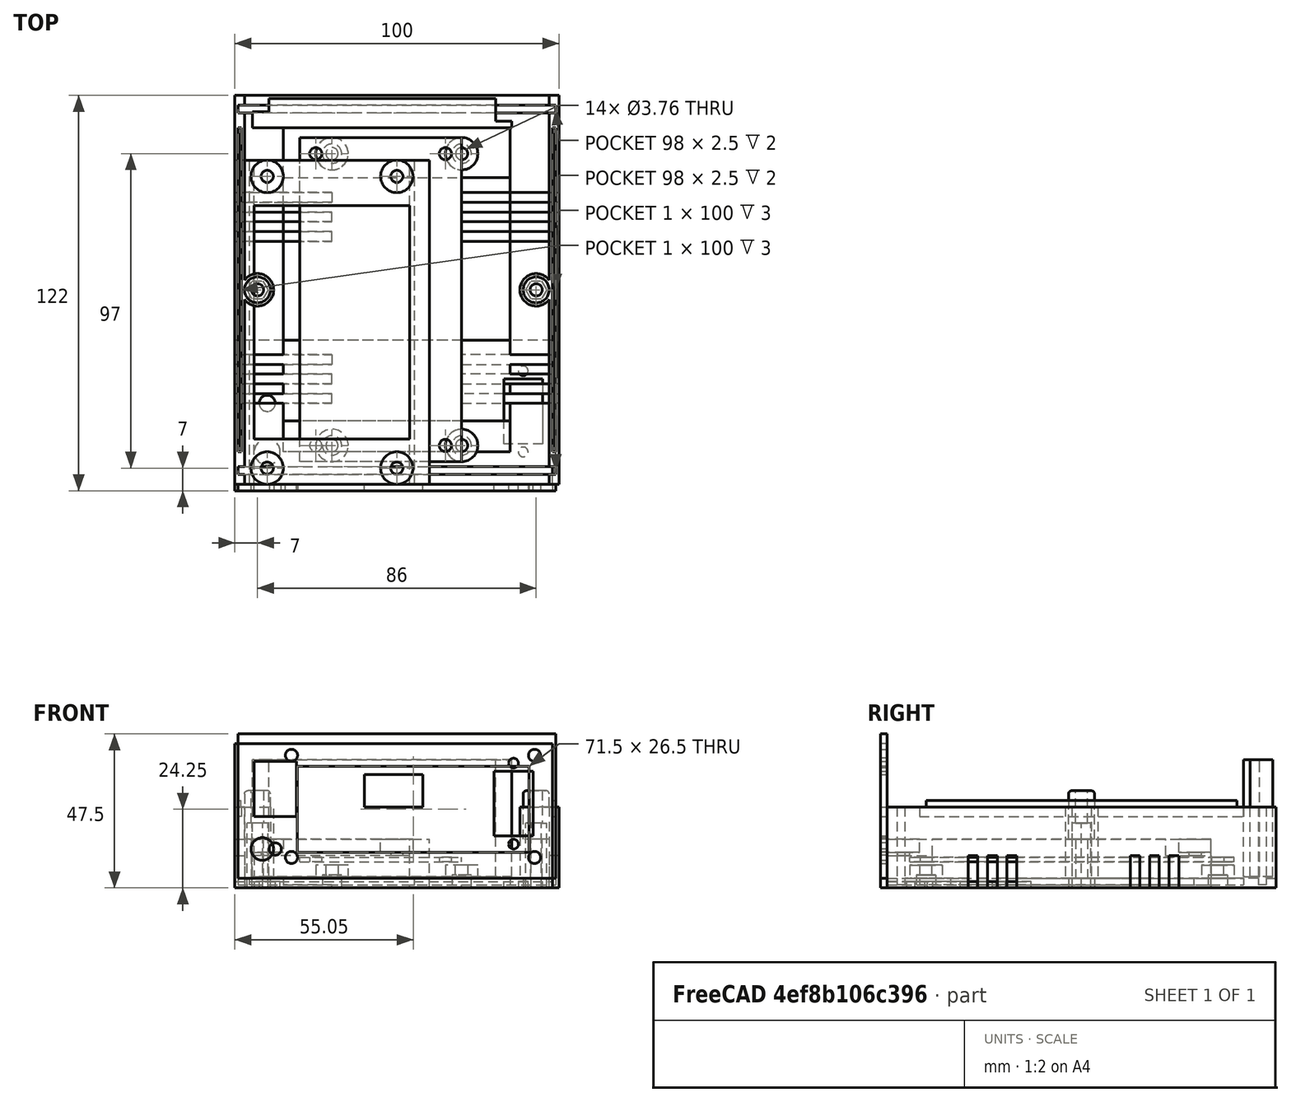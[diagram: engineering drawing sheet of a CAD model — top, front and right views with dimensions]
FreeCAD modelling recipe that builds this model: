
FCSTD DOCUMENT  (FreeCAD 0.18R)
Label: Gehäuse_mit_Display
License: All rights reserved
LicenseURL: http://en.wikipedia.org/wiki/All_rights_reserved
objects: Sketcher::SketchObject×35, PartDesign::Pocket×24, PartDesign::Pad×12, PartDesign::Body×9, PartDesign::Plane×8, PartDesign::FeatureBase×2, Spreadsheet::Sheet×1, PartDesign::Fillet×1
note: 127 computed .brp shape members not serialized (recipe doc carries the construction recipe); baked Part::Feature solids carry a one-line shape summary decoded from their .brp

FEATURE [Sketcher::SketchObject] Sketch
  MapMode = 5
  Support = -> [XY_Plane]
  expr: Constraints.Grund_X = Parameter.Breite
  expr: Constraints.Grund_Y = Parameter.Tiefe
  sketch-geometry (4):
    g0: LineSegment StartX=0 StartY=120 StartZ=0 EndX=100 EndY=120 EndZ=0
    g1: LineSegment StartX=100 StartY=120 StartZ=0 EndX=100 EndY=0 EndZ=0
    g2: LineSegment StartX=100 StartY=0 StartZ=0 EndX=0 EndY=0 EndZ=0
    g3: LineSegment StartX=0 StartY=0 StartZ=0 EndX=0 EndY=120 EndZ=0
  constraints (11):
    c: Coincident(g0,g1)
    c: Coincident(g1,g2)
    c: Coincident(g2,g3)
    c: Coincident(g3,g0)
    c: Horizontal(g2)
    c: Vertical(g1)
    c: DistanceY(g2,g0) = 120  'Grund_Y'
    c: DistanceX(g2,g1) = 100  'Grund_X'
    c: Vertical(g3)
    c: Horizontal(g0)
    c: Coincident(g-1,g2)
FEATURE [Spreadsheet::Sheet] Spreadsheet  label="Parameter"
  cells = A1=Breite (X); B1(Breite)=100; A2=Tiefe (Y); B2(Tiefe)=120; A3=Höhe (Z); B3(Hoehe)=25; A4=Wandstärke; B4(Wandstaerke)=3; A5=Wandstärke Frontblende; B5(Wandstaerke_Frontblende)=2.5; A6=Breite der Nut / Feder zwischen Ober und Unterteil; B6(Nut_Feder_Breite)=1; A7=Faktor Breite Feder zwischen Ober-und Unterteil; B7(Nut_Feder_Breite_Faktor_Unterteil)=0.90000000000000002; A8=Start der Nut von der Front- Heckansicht; B8(Nut_Feder_Entfernung_Vorne_Hinten)=10; A9=Entfernung Schalenverschraubung zur Innenwand; B9(Abstand_Verschraubung_Innen)=4; A10=Breite Platine; B10(Platine_Breite)=50; A11=Tiefe Platine; B11(Platine_Tiefe)=100; A12=Abstand Bohrlöcher Platine zum Außenrand; B12(Platine_Abstand_Bohrloch_Aussenrand)=5; A13=Breite Luftschlitz Boden; B13(Luftschlitz_Breite_Boden)=30; A14=Tiefe Luftschlitz Boden; B14(Luftschlitz_Tiefe_Boden)=3; A15=Höhe Luftschlitz Boden; B15(Luftschlitz_Hoehe_Boden)=10; A17=Helper; A18=Abstand Schalenverschraubung außen; B18(Helper_Abstand_Schalenverschraubung_Aussen)==Abstand_Verschraubung_Innen + Wandstaerke; A19=Breite Feder Unterteil; B19(Helper_Nut_Feder_Breite_Unterteil)==Parameter.Nut_Feder_Breite * Parameter.Nut_Feder_Breite_Faktor_Unterteil
FEATURE [PartDesign::Pad] Pad  label="Grundkörper"
  Length = 25
  Length2 = 100
  Profile = -> Sketch
  Type = 0
  expr: Length = Parameter.Hoehe
FEATURE [Sketcher::SketchObject] Sketch002
  MapMode = 5
  Support = -> [XY_Plane001]
  sketch-geometry (8):
    g0: LineSegment StartX=0 StartY=0 StartZ=0 EndX=80 EndY=0 EndZ=0
    g1: LineSegment StartX=80 StartY=0 StartZ=0 EndX=80 EndY=2 EndZ=0
    g2: LineSegment StartX=80 StartY=2 StartZ=0 EndX=75 EndY=2 EndZ=0
    g3: LineSegment StartX=75 StartY=2 StartZ=0 EndX=75 EndY=9 EndZ=0
    g4: LineSegment StartX=75 StartY=9 StartZ=0 EndX=5 EndY=9 EndZ=0
    g5: LineSegment StartX=5 StartY=9 StartZ=0 EndX=5 EndY=5 EndZ=0
    g6: LineSegment StartX=5 StartY=5 StartZ=0 EndX=0 EndY=5 EndZ=0
    g7: LineSegment StartX=0 StartY=5 StartZ=0 EndX=0 EndY=0 EndZ=0
  constraints (23):
    c: Horizontal(g0)
    c: Coincident(g0,g1)
    c: Coincident(g1,g2)
    c: Horizontal(g2)
    c: Coincident(g2,g3)
    c: Vertical(g3)
    c: Coincident(g3,g4)
    c: Horizontal(g4)
    c: Coincident(g4,g5)
    c: Vertical(g5)
    c: Coincident(g5,g6)
    c: Horizontal(g6)
    c: Coincident(g6,g7)
    c: Coincident(g7,g0)
    c: Vertical(g7)
    c: DistanceY(g0,g6) = 5
    c: DistanceY(g0,g1) = 2
    c: DistanceX(g0,g0) = 80
    c: Vertical(g1)
    c: DistanceX(g4,g3) = 70
    c: DistanceY(g2,g3) = 7
    c: DistanceX(g6,g5) = 5
    c: Coincident(g-1,g0)
FEATURE [PartDesign::Pad] Pad001
  Length = 35
  Length2 = 100
  Profile = -> Sketch002
  Type = 0
FEATURE [PartDesign::Pad] Pad002
  BaseFeature = -> Pad001
  Length = 36
  Length2 = 100
  Profile = -> Sketch002
  Type = 0
FEATURE [PartDesign::Body] Body001  label="LCD1602 Display"
  Group = -> [Sketch002,Pad001,Pad002]
  Origin = -> Origin001
  Placement = pos=(5.5,110,3.5) rot=(0,0,1;0rad)
  Tip = -> Pad002
FEATURE [Sketcher::SketchObject] Sketch003
  MapMode = 5
  Placement = pos=(0,0,0) rot=(1,0,0;1.5708rad)
  Support = -> [XZ_Plane]
  expr: Constraints[11] = Parameter.Hoehe - 1 * Parameter.Wandstaerke
  expr: Constraints[10] = Parameter.Wandstaerke
  expr: Constraints[9] = Parameter.Breite - 2 * Parameter.Wandstaerke
  expr: Constraints[8] = Parameter.Wandstaerke
  sketch-geometry (4):
    g0: LineSegment StartX=3 StartY=25 StartZ=0 EndX=97 EndY=25 EndZ=0
    g1: LineSegment StartX=97 StartY=25 StartZ=0 EndX=97 EndY=3 EndZ=0
    g2: LineSegment StartX=97 StartY=3 StartZ=0 EndX=3 EndY=3 EndZ=0
    g3: LineSegment StartX=3 StartY=3 StartZ=0 EndX=3 EndY=25 EndZ=0
  constraints (12):
    c: Coincident(g0,g1)
    c: Coincident(g1,g2)
    c: Coincident(g2,g3)
    c: Coincident(g3,g0)
    c: Horizontal(g0)
    c: Horizontal(g2)
    c: Vertical(g1)
    c: Vertical(g3)
    c: DistanceX(g-1,g2) = 3
    c: DistanceX(g2,g1) = 94
    c: DistanceY(g-1,g2) = 3
    c: DistanceY(g1,g0) = 22
FEATURE [Sketcher::SketchObject] Sketch001
  MapMode = 5
  Placement = pos=(0,0,25) rot=(0,0,1;0rad)
  Support = -> [Pad]
  expr: Constraints[39] = Parameter.Wandstaerke_Frontblende
  expr: Constraints[21] = Parameter.Breite
  expr: Constraints[31] = Parameter.Wandstaerke
  expr: Constraints[50] = Parameter.Wandstaerke_Frontblende
  expr: Constraints[36] = Parameter.Wandstaerke
  expr: Constraints[34] = Parameter.Wandstaerke
  expr: Constraints[58] = Parameter.Wandstaerke_Frontblende
  expr: Constraints[20] = Parameter.Tiefe
  expr: Constraints[38] = Parameter.Wandstaerke
  expr: Constraints[37] = Parameter.Wandstaerke
  expr: Constraints[35] = Parameter.Wandstaerke
  expr: Constraints[56] = Parameter.Wandstaerke_Frontblende
  expr: Constraints[23] = Parameter.Wandstaerke
  sketch-geometry (20):
    g0: LineSegment StartX=3 StartY=117 StartZ=0 EndX=1 EndY=117 EndZ=0
    g1: LineSegment StartX=1 StartY=117 StartZ=0 EndX=1 EndY=114.5 EndZ=0
    g2: LineSegment StartX=1 StartY=114.5 StartZ=0 EndX=3 EndY=114.5 EndZ=0
    g3: LineSegment StartX=3 StartY=5.5 StartZ=0 EndX=1 EndY=5.5 EndZ=0
    g4: LineSegment StartX=1 StartY=5.5 StartZ=0 EndX=1 EndY=3 EndZ=0
    g5: LineSegment StartX=1 StartY=3 StartZ=0 EndX=3 EndY=3 EndZ=0
    g6: LineSegment StartX=3 StartY=3 StartZ=0 EndX=97 EndY=3 EndZ=0
    g7: LineSegment StartX=97 StartY=3 StartZ=0 EndX=99 EndY=3 EndZ=0
    g8: LineSegment StartX=99 StartY=3 StartZ=0 EndX=99 EndY=5.5 EndZ=0
    g9: LineSegment StartX=99 StartY=5.5 StartZ=0 EndX=97 EndY=5.5 EndZ=0
    g10: LineSegment StartX=97 StartY=114.5 StartZ=0 EndX=99 EndY=114.5 EndZ=0
    g11: LineSegment StartX=99 StartY=114.5 StartZ=0 EndX=99 EndY=117 EndZ=0
    g12: LineSegment StartX=99 StartY=117 StartZ=0 EndX=97 EndY=117 EndZ=0
    g13: LineSegment StartX=97 StartY=117 StartZ=0 EndX=3 EndY=117 EndZ=0
    g14: LineSegment [constr] StartX=-3e-16 StartY=0 StartZ=0 EndX=100 EndY=0 EndZ=0
    g15: LineSegment [constr] StartX=100 StartY=0 StartZ=0 EndX=100 EndY=120 EndZ=0
    g16: LineSegment [constr] StartX=100 StartY=120 StartZ=0 EndX=0 EndY=120 EndZ=0
    g17: LineSegment StartX=3 StartY=114.5 StartZ=0 EndX=3 EndY=5.5 EndZ=0
    g18: LineSegment StartX=97 StartY=114.5 StartZ=0 EndX=97 EndY=5.5 EndZ=0
    g19: LineSegment [constr] StartX=0 StartY=120 StartZ=0 EndX=0 EndY=0 EndZ=0
  constraints (59):
    c: Coincident(g0,g1)
    c: Vertical(g1)
    c: Coincident(g1,g2)
    c: Horizontal(g2)
    c: Horizontal(g3)
    c: Coincident(g3,g4)
    c: Vertical(g4)
    c: Coincident(g4,g5)
    c: Horizontal(g6)
    c: Horizontal(g7)
    c: Coincident(g7,g8)
    c: Coincident(g8,g9)
    c: Horizontal(g10)
    c: Coincident(g10,g11)
    c: Coincident(g11,g12)
    c: Horizontal(g13)
    c: Coincident(g14,g15)
    c: Coincident(g15,g16)
    c: Horizontal(g14)
    c: Horizontal(g16)
    c: DistanceY(g14,g15) = 120
    c: DistanceX(g16,g15) = 100
    c: Coincident(g14,g-1)
    c: DistanceY(g-1,g6) = 3
    c: Horizontal(g5)
    c: Horizontal(g12)
    c: Vertical(g11)
    c: Vertical(g8)
    c: DistanceX(g-1,g4) = 1
    c: DistanceX(g16,g0) = 1
    c: Horizontal(g0)
    c: DistanceX(g-1,g3) = 3
    c: DistanceX(g7,g14) = 1
    c: Horizontal(g9)
    c: DistanceX(g9,g14) = 3
    c: DistanceX(g-1,g6) = 3
    c: DistanceX(g6,g14) = 3
    c: DistanceX(g16,g13) = 3
    c: DistanceX(g13,g15) = 3
    c: DistanceY(g2,g0) = 2.5
    c: Vertical(g17)
    c: Coincident(g2,g17)
    c: Coincident(g18,g10)
    c: Coincident(g18,g9)
    c: Vertical(g18)
    c: Equal(g16,g14)
    c: Coincident(g17,g3)
    c: Coincident(g19,g-1)
    c: Coincident(g19,g16)
    c: DistanceX(g11,g15) = 1
    c: DistanceY(g10,g11) = 2.5
    c: Equal(g0,g2)
    c: DistanceY(g0,g16) = 3
    c: Coincident(g13,g0)
    c: Coincident(g13,g12)
    c: Coincident(g5,g6)
    c: DistanceY(g4,g3) = 2.5
    c: Coincident(g7,g6)
    c: DistanceY(g7,g8) = 2.5
FEATURE [PartDesign::Pocket] Pocket  label="Innenraum"
  BaseFeature = -> Pad
  Length = 22
  Length2 = 100
  Profile = -> Sketch001
  Type = 0
  expr: Length = Parameter.Hoehe - Parameter.Wandstaerke
FEATURE [PartDesign::Pocket] Pocket001  label="Öffnung vorn und hinten"
  BaseFeature = -> Pocket
  Length = 5
  Length2 = 100
  Profile = -> Sketch003
  Type = 1
FEATURE [Sketcher::SketchObject] Sketch005
  MapMode = 5
  Placement = pos=(0,0,3) rot=(0,0,1;0rad)
  Support = -> [Pocket001]
  expr: Constraints[23] = Parameter.Wandstaerke
  expr: Constraints[21] = Parameter.Wandstaerke_Frontblende
  expr: Constraints[11] = Parameter.Tiefe - Parameter.Wandstaerke_Frontblende - Parameter.Wandstaerke
  expr: Constraints[10] = Parameter.Wandstaerke_Frontblende
  expr: Constraints[22] = Parameter.Breite - 2
  expr: Constraints[9] = Parameter.Breite - 2
  sketch-geometry (8):
    g0: LineSegment StartX=1 StartY=117 StartZ=0 EndX=99 EndY=117 EndZ=0
    g1: LineSegment StartX=99 StartY=117 StartZ=0 EndX=99 EndY=114.5 EndZ=0
    g2: LineSegment StartX=99 StartY=114.5 StartZ=0 EndX=1 EndY=114.5 EndZ=0
    g3: LineSegment StartX=1 StartY=114.5 StartZ=0 EndX=1 EndY=117 EndZ=0
    g4: LineSegment StartX=1 StartY=5.5 StartZ=0 EndX=99 EndY=5.5 EndZ=0
    g5: LineSegment StartX=99 StartY=5.5 StartZ=0 EndX=99 EndY=3 EndZ=0
    g6: LineSegment StartX=99 StartY=3 StartZ=0 EndX=1 EndY=3 EndZ=0
    g7: LineSegment StartX=1 StartY=3 StartZ=0 EndX=1 EndY=5.5 EndZ=0
  constraints (24):
    c: Coincident(g0,g1)
    c: Coincident(g1,g2)
    c: Coincident(g2,g3)
    c: Coincident(g3,g0)
    c: Horizontal(g0)
    c: Horizontal(g2)
    c: Vertical(g1)
    c: Vertical(g3)
    c: DistanceX(g-1,g2) = 1
    c: DistanceX(g0,g0) = 98
    c: DistanceY(g2,g0) = 2.5
    c: DistanceY(g-1,g2) = 114.5
    c: Coincident(g4,g5)
    c: Coincident(g5,g6)
    c: Coincident(g6,g7)
    c: Coincident(g7,g4)
    c: Horizontal(g4)
    c: Horizontal(g6)
    c: Vertical(g5)
    c: Vertical(g7)
    c: DistanceX(g-1,g6) = 1
    c: DistanceY(g5,g4) = 2.5
    c: DistanceX(g6,g5) = 98
    c: DistanceY(g-1,g6) = 3
FEATURE [Sketcher::SketchObject] Sketch006
  MapMode = 5
  Support = -> [XY_Plane002]
  sketch-geometry (4):
    g0: LineSegment StartX=0 StartY=100 StartZ=0 EndX=50 EndY=100 EndZ=0
    g1: LineSegment StartX=50 StartY=100 StartZ=0 EndX=50 EndY=0 EndZ=0
    g2: LineSegment StartX=50 StartY=0 StartZ=0 EndX=0 EndY=0 EndZ=0
    g3: LineSegment StartX=0 StartY=0 StartZ=0 EndX=0 EndY=100 EndZ=0
  constraints (11):
    c: Coincident(g0,g1)
    c: Coincident(g1,g2)
    c: Coincident(g2,g3)
    c: Coincident(g3,g0)
    c: Horizontal(g0)
    c: Horizontal(g2)
    c: Vertical(g1)
    c: Vertical(g3)
    c: DistanceY(g1,g0) = 100
    c: DistanceX(g2,g1) = 50
    c: Coincident(g-1,g2)
FEATURE [PartDesign::Pad] Pad003  label="Grundplatte"
  Length = 1.5
  Length2 = 100
  Profile = -> Sketch006
  Type = 0
FEATURE [Sketcher::SketchObject] Sketch008
  MapMode = 5
  Support = -> [XY_Plane002]
  sketch-geometry (12):
    g0: Circle CenterX=45 CenterY=95 CenterZ=0 NormalX=0 NormalY=0 NormalZ=1 AngleXU=0 Radius=1.88
    g1: Circle CenterX=5 CenterY=5 CenterZ=0 NormalX=0 NormalY=0 NormalZ=1 AngleXU=0 Radius=1.88
    g2: Circle CenterX=45 CenterY=5 CenterZ=0 NormalX=0 NormalY=0 NormalZ=1 AngleXU=0 Radius=1.88
    g3: LineSegment [constr] StartX=0 StartY=100 StartZ=0 EndX=50 EndY=100 EndZ=0
    g4: LineSegment [constr] StartX=50 StartY=100 StartZ=0 EndX=50 EndY=0 EndZ=0
    g5: LineSegment [constr] StartX=50 StartY=0 StartZ=0 EndX=0 EndY=0 EndZ=0
    g6: LineSegment [constr] StartX=0 StartY=0 StartZ=0 EndX=0 EndY=100 EndZ=0
    g7: LineSegment [constr] StartX=5 StartY=95 StartZ=0 EndX=45 EndY=95 EndZ=0
    g8: LineSegment [constr] StartX=45 StartY=95 StartZ=0 EndX=45 EndY=5 EndZ=0
    g9: LineSegment [constr] StartX=45 StartY=5 StartZ=0 EndX=5 EndY=5 EndZ=0
    g10: LineSegment [constr] StartX=5 StartY=5 StartZ=0 EndX=5 EndY=95 EndZ=0
    g11: Circle CenterX=5 CenterY=95 CenterZ=0 NormalX=0 NormalY=0 NormalZ=1 AngleXU=0 Radius=1.88
  constraints (31):
    c: Coincident(g3,g4)
    c: Coincident(g4,g5)
    c: Coincident(g5,g6)
    c: Coincident(g6,g3)
    c: Horizontal(g3)
    c: Horizontal(g5)
    c: Vertical(g4)
    c: Vertical(g6)
    c: Coincident(g5,g-1)
    c: DistanceY(g4,g3) = 100
    c: DistanceX(g-1,g4) = 50
    c: Coincident(g7,g8)
    c: Coincident(g8,g9)
    c: Coincident(g9,g10)
    c: Coincident(g10,g7)
    c: Horizontal(g7)
    c: Horizontal(g9)
    c: Vertical(g8)
    c: Vertical(g10)
    c: Coincident(g1,g9)
    c: Coincident(g8,g2)
    c: Coincident(g0,g7)
    c: DistanceX(g-1,g1) = 5
    c: DistanceY(g-1,g1) = 5
    c: DistanceX(g1,g2) = 40
    c: Coincident(g7,g11)
    c: Radius(g11) = 1.88
    c: Equal(g11,g0)
    c: Equal(g11,g1)
    c: Equal(g11,g2)
    c: DistanceY(g11,g3) = 5
FEATURE [PartDesign::Pocket] Pocket003  label="Befestigung M3"
  BaseFeature = -> Pad003
  Length = 12
  Length2 = 100
  Profile = -> Sketch008
  Reversed = true
  Type = 1
FEATURE [PartDesign::Body] Body002  label="Board"
  Group = -> [Sketch006,Pad003,Sketch008,Pocket003]
  Origin = -> Origin002
  Placement = pos=(20,7,8) rot=(0,0,1;0rad)
  Tip = -> Pocket003
FEATURE [Sketcher::SketchObject] Sketch010
  MapMode = 5
  Placement = pos=(-2e-16,-1.8e-15,7) rot=(0,0,1;0rad)
  expr: Constraints[11] = Parameter.Platine_Breite - 2 * Parameter.Platine_Abstand_Bohrloch_Aussenrand
  expr: Constraints[10] = Parameter.Platine_Tiefe - 2 * Parameter.Platine_Abstand_Bohrloch_Aussenrand
  expr: Constraints[8] = (Parameter.Breite - (Parameter.Platine_Breite - 2 * Parameter.Platine_Abstand_Bohrloch_Aussenrand)) / 2
  sketch-geometry (8):
    g0: LineSegment [constr] StartX=30 StartY=102 StartZ=0 EndX=70 EndY=102 EndZ=0
    g1: LineSegment [constr] StartX=70 StartY=102 StartZ=0 EndX=70 EndY=12 EndZ=0
    g2: LineSegment [constr] StartX=70 StartY=12 StartZ=0 EndX=30 EndY=12 EndZ=0
    g3: LineSegment [constr] StartX=30 StartY=12 StartZ=0 EndX=30 EndY=102 EndZ=0
    g4: Circle CenterX=30 CenterY=102 CenterZ=0 NormalX=0 NormalY=0 NormalZ=1 AngleXU=0 Radius=1.88
    g5: Circle CenterX=70 CenterY=102 CenterZ=0 NormalX=0 NormalY=0 NormalZ=1 AngleXU=0 Radius=1.88
    g6: Circle CenterX=30 CenterY=12 CenterZ=0 NormalX=0 NormalY=0 NormalZ=1 AngleXU=0 Radius=1.88
    g7: Circle CenterX=70 CenterY=12 CenterZ=0 NormalX=0 NormalY=0 NormalZ=1 AngleXU=0 Radius=1.88
  constraints (20):
    c: Coincident(g0,g1)
    c: Coincident(g1,g2)
    c: Coincident(g2,g3)
    c: Coincident(g3,g0)
    c: Horizontal(g0)
    c: Horizontal(g2)
    c: Vertical(g1)
    c: Vertical(g3)
    c: DistanceX(g-1,g2) = 30
    c: DistanceY(g-1,g2) = 12
    c: DistanceY(g1,g0) = 90
    c: DistanceX(g0,g0) = 40
    c: Equal(g4,g5)
    c: Equal(g4,g6)
    c: Equal(g4,g7)
    c: Radius(g4) = 1.88
    c: Coincident(g0,g4)
    c: Coincident(g0,g5)
    c: Coincident(g1,g7)
    c: Coincident(g2,g6)
FEATURE [PartDesign::Plane] DatumPlane  label="Ebene Boden innen"
  Length = 133.917
  MapMode = 5
  Placement = pos=(0,0,3) rot=(0,0,1;0rad)
  ResizeMode = 0
  Support = -> [Pocket001]
  Width = 153.917
FEATURE [Sketcher::SketchObject] Sketch009
  MapMode = 5
  Placement = pos=(0,0,3) rot=(0,0,1;0rad)
  Support = -> [DatumPlane]
  expr: Constraints[18] = Parameter.Helper_Abstand_Schalenverschraubung_Aussen
  expr: Constraints[3] = Parameter.Helper_Abstand_Schalenverschraubung_Aussen
  expr: Constraints[17] = Parameter.Tiefe
  expr: Constraints[16] = Parameter.Breite
  expr: Constraints[2] = Parameter.Tiefe / 2
  sketch-geometry (7):
    g0: Circle CenterX=7 CenterY=60 CenterZ=0 NormalX=0 NormalY=0 NormalZ=1 AngleXU=0 Radius=5
    g1: Circle CenterX=93 CenterY=60 CenterZ=0 NormalX=0 NormalY=0 NormalZ=1 AngleXU=0 Radius=5
    g2: LineSegment [constr] StartX=7 StartY=60 StartZ=0 EndX=93 EndY=60 EndZ=0
    g3: LineSegment [constr] StartX=0 StartY=120 StartZ=0 EndX=100 EndY=120 EndZ=0
    g4: LineSegment [constr] StartX=100 StartY=120 StartZ=0 EndX=100 EndY=0 EndZ=0
    g5: LineSegment [constr] StartX=100 StartY=0 StartZ=0 EndX=0 EndY=0 EndZ=0
    g6: LineSegment [constr] StartX=0 StartY=0 StartZ=0 EndX=0 EndY=120 EndZ=0
  constraints (19):
    c: Radius(g0) = 5
    c: Horizontal(g2)
    c: DistanceY(g-1,g2) = 60
    c: DistanceX(g-1,g2) = 7
    c: Coincident(g2,g0)
    c: Coincident(g1,g2)
    c: Equal(g0,g1)
    c: Coincident(g3,g4)
    c: Coincident(g4,g5)
    c: Coincident(g5,g6)
    c: Coincident(g6,g3)
    c: Horizontal(g3)
    c: Horizontal(g5)
    c: Vertical(g4)
    c: Vertical(g6)
    c: Coincident(g5,g-1)
    c: DistanceX(g-1,g4) = 100
    c: DistanceY(g4,g3) = 120
    c: DistanceX(g1,g4) = 7
FEATURE [PartDesign::Pad] Pad007  label="Gehäuseverschraubung"
  BaseFeature = -> Pocket001
  Length = 22
  Length2 = 100
  Profile = -> Sketch009
  Type = 0
  expr: Length = Parameter.Hoehe - Parameter.Wandstaerke
FEATURE [PartDesign::Plane] DatumPlane001  label="Ebene Unterseite001"
  Length = 133.917
  MapMode = 5
  Placement = pos=(0,0,0) rot=(1,0,0;3.14159rad)
  ResizeMode = 0
  Support = -> [Pad007]
  Width = 153.917
FEATURE [PartDesign::Plane] DatumPlane002  label="Ebene Abstandhalter Platine"
  Length = 133.917
  MapMode = 5
  Placement = pos=(0,0,7) rot=(0,0,1;0rad)
  ResizeMode = 0
  Width = 153.917
FEATURE [PartDesign::Plane] DatumPlane004  label="Ebene Fixierung Oberschale"
  Length = 133.917
  MapMode = 5
  Placement = pos=(0,0,30) rot=(0,0,1;0rad)
  ResizeMode = 0
  Width = 153.917
FEATURE [Sketcher::SketchObject] Sketch012
  MapMode = 5
  Placement = pos=(0,0,30) rot=(0,0,1;0rad)
  Support = -> [DatumPlane004]
  expr: Constraints[13] = Parameter.Helper_Abstand_Schalenverschraubung_Aussen
  expr: Constraints[12] = Parameter.Helper_Abstand_Schalenverschraubung_Aussen
  expr: Constraints[10] = Parameter.Breite
  expr: Constraints[14] = Parameter.Tiefe / 2
  expr: Constraints[9] = Parameter.Tiefe
  sketch-geometry (7):
    g0: LineSegment [constr] StartX=0 StartY=120 StartZ=0 EndX=100 EndY=120 EndZ=0
    g1: LineSegment [constr] StartX=100 StartY=120 StartZ=0 EndX=100 EndY=0 EndZ=0
    g2: LineSegment [constr] StartX=100 StartY=0 StartZ=0 EndX=0 EndY=0 EndZ=0
    g3: LineSegment [constr] StartX=0 StartY=0 StartZ=0 EndX=0 EndY=120 EndZ=0
    g4: LineSegment [constr] StartX=7 StartY=60 StartZ=0 EndX=93 EndY=60 EndZ=0
    g5: Circle CenterX=7 CenterY=60 CenterZ=0 NormalX=0 NormalY=0 NormalZ=1 AngleXU=0 Radius=1.88
    g6: Circle CenterX=93 CenterY=60 CenterZ=0 NormalX=0 NormalY=0 NormalZ=1 AngleXU=0 Radius=1.88
  constraints (19):
    c: Coincident(g0,g1)
    c: Coincident(g1,g2)
    c: Coincident(g2,g3)
    c: Coincident(g3,g0)
    c: Horizontal(g0)
    c: Horizontal(g2)
    c: Vertical(g1)
    c: Vertical(g3)
    c: Coincident(g-1,g2)
    c: DistanceY(g-1,g0) = 120
    c: DistanceX(g-1,g1) = 100
    c: Horizontal(g4)
    c: DistanceX(g-1,g4) = 7
    c: DistanceX(g4,g1) = 7
    c: DistanceY(g-1,g4) = 60
    c: Coincident(g5,g4)
    c: Coincident(g6,g4)
    c: Equal(g5,g6)
    c: Radius(g5) = 1.88
FEATURE [PartDesign::Pocket] Pocket011  label="Fase"
  BaseFeature = -> Pad007
  Length = 2
  Length2 = 100
  Profile = -> Sketch005
  Type = 0
FEATURE [PartDesign::Body] Body  label="Gehäuseschale Basis"
  Group = -> [Sketch,Pad,Sketch001,Sketch003,Pocket,Pocket001,DatumPlane,Sketch009,Sketch005,Pad007,DatumPlane001,Pocket011]
  Origin = -> Origin
  Tip = -> Pocket011
FEATURE [PartDesign::FeatureBase] BaseFeature
  BaseFeature = -> Body
FEATURE [Sketcher::SketchObject] Sketch007
  MapMode = 5
  Placement = pos=(0,0,3) rot=(0,0,1;0rad)
  Support = -> [BaseFeature]
  expr: Constraints[17] = Parameter.Platine_Breite - 2 * Parameter.Platine_Abstand_Bohrloch_Aussenrand
  expr: Constraints[16] = Parameter.Platine_Tiefe - 2 * Parameter.Platine_Abstand_Bohrloch_Aussenrand
  expr: Constraints[18] = (Parameter.Breite - 40) / 2
  sketch-geometry (8):
    g0: Circle CenterX=30 CenterY=12 CenterZ=0 NormalX=0 NormalY=0 NormalZ=1 AngleXU=0 Radius=5
    g1: Circle CenterX=70 CenterY=12 CenterZ=0 NormalX=0 NormalY=0 NormalZ=1 AngleXU=0 Radius=5
    g2: Circle CenterX=30 CenterY=102 CenterZ=0 NormalX=0 NormalY=0 NormalZ=1 AngleXU=0 Radius=5
    g3: Circle CenterX=70 CenterY=102 CenterZ=0 NormalX=0 NormalY=0 NormalZ=1 AngleXU=0 Radius=5
    g4: LineSegment [constr] StartX=30 StartY=102 StartZ=0 EndX=70 EndY=102 EndZ=0
    g5: LineSegment [constr] StartX=70 StartY=102 StartZ=0 EndX=70 EndY=12 EndZ=0
    g6: LineSegment [constr] StartX=70 StartY=12 StartZ=0 EndX=30 EndY=12 EndZ=0
    g7: LineSegment [constr] StartX=30 StartY=12 StartZ=0 EndX=30 EndY=102 EndZ=0
  constraints (20):
    c: Radius(g0) = 5
    c: Equal(g0,g2)
    c: Equal(g0,g3)
    c: Equal(g1,g0)
    c: Coincident(g4,g5)
    c: Coincident(g5,g6)
    c: Coincident(g6,g7)
    c: Coincident(g7,g4)
    c: Horizontal(g4)
    c: Horizontal(g6)
    c: Vertical(g5)
    c: Vertical(g7)
    c: Coincident(g1,g5)
    c: Coincident(g0,g6)
    c: Coincident(g4,g2)
    c: Coincident(g4,g3)
    c: DistanceY(g1,g3) = 90
    c: DistanceX(g2,g3) = 40
    c: DistanceX(g-1,g0) = 30
    c: DistanceY(g-1,g0) = 12
FEATURE [PartDesign::Pad] Pad009
  BaseFeature = -> BaseFeature
  Length = 4
  Length2 = 100
  Profile = -> Sketch007
  Type = 0
FEATURE [PartDesign::Pocket] Pocket006  label="Board Befestigungsschrauben"
  BaseFeature = -> Pad009
  Length = 5
  Length2 = 100
  Profile = -> Sketch010
  Type = 1
FEATURE [PartDesign::Plane] DatumPlane003  label="Ebene Verschraubung Ober- und Unterteil"
  Length = 133.917
  MapMode = 5
  Placement = pos=(0,0,1) rot=(0,0,1;0rad)
  ResizeMode = 0
  Support = -> [Pocket006]
  Width = 153.917
FEATURE [Sketcher::SketchObject] Sketch016
  MapMode = 5
  Placement = pos=(0,0,0) rot=(1,0,0;1.5708rad)
  Support = -> [XZ_Plane004]
  expr: Constraints[10] = 2 * Parameter.Hoehe - 2 * Parameter.Wandstaerke + 0.5
  expr: Constraints[9] = Parameter.Breite - 2
  sketch-geometry (4):
    g0: LineSegment StartX=0 StartY=44.5 StartZ=0 EndX=98 EndY=44.5 EndZ=0
    g1: LineSegment StartX=98 StartY=44.5 StartZ=0 EndX=98 EndY=0 EndZ=0
    g2: LineSegment StartX=98 StartY=0 StartZ=0 EndX=0 EndY=0 EndZ=0
    g3: LineSegment StartX=0 StartY=0 StartZ=0 EndX=0 EndY=44.5 EndZ=0
  constraints (11):
    c: Coincident(g0,g1)
    c: Coincident(g1,g2)
    c: Coincident(g2,g3)
    c: Coincident(g3,g0)
    c: Horizontal(g0)
    c: Horizontal(g2)
    c: Vertical(g1)
    c: Vertical(g3)
    c: Coincident(g-1,g2)
    c: DistanceX(g2,g1) = 98
    c: DistanceY(g1,g0) = 44.5
FEATURE [PartDesign::Pad] Pad011  label="Frontplatte"
  Length = 2
  Length2 = 100
  Placement = pos=(0,0,0) rot=(1,0,0;1.5708rad)
  Profile = -> Sketch016
  Type = 0
FEATURE [Sketcher::SketchObject] Sketch017
  MapMode = 5
  Placement = pos=(0,0,0) rot=(1,0,0;1.5708rad)
  Support = -> [XZ_Plane004]
  sketch-geometry (17):
    g0: LineSegment [constr] StartX=14 StartY=40.4 StartZ=0 EndX=94 EndY=40.4 EndZ=0
    g1: LineSegment [constr] StartX=94 StartY=40.4 StartZ=0 EndX=94 EndY=2 EndZ=0
    g2: LineSegment [constr] StartX=94 StartY=2 StartZ=0 EndX=14 EndY=2 EndZ=0
    g3: LineSegment [constr] StartX=14 StartY=2 StartZ=0 EndX=14 EndY=40.4 EndZ=0
    g4: Circle CenterX=16.5 CenterY=37.9 CenterZ=0 NormalX=0 NormalY=0 NormalZ=1 AngleXU=0 Radius=1.88
    g5: Circle CenterX=91.5 CenterY=37.9 CenterZ=0 NormalX=0 NormalY=0 NormalZ=1 AngleXU=0 Radius=1.88
    g6: Circle CenterX=16.5 CenterY=6.4 CenterZ=0 NormalX=0 NormalY=0 NormalZ=1 AngleXU=0 Radius=1.88
    g7: Circle CenterX=91.5 CenterY=6.4 CenterZ=0 NormalX=0 NormalY=0 NormalZ=1 AngleXU=0 Radius=1.88
    g8: LineSegment [constr] StartX=16.5 StartY=37.9 StartZ=0 EndX=91.5 EndY=37.9 EndZ=0
    g9: LineSegment [constr] StartX=91.5 StartY=37.9 StartZ=0 EndX=91.5 EndY=6.4 EndZ=0
    g10: LineSegment [constr] StartX=91.5 StartY=6.4 StartZ=0 EndX=16.5 EndY=6.4 EndZ=0
    g11: LineSegment [constr] StartX=16.5 StartY=6.4 StartZ=0 EndX=16.5 EndY=37.9 EndZ=0
    g12: LineSegment StartX=18.3 StartY=34.5 StartZ=0 EndX=89.8 EndY=34.5 EndZ=0
    g13: LineSegment StartX=89.8 StartY=34.5 StartZ=0 EndX=89.8 EndY=8 EndZ=0
    g14: LineSegment StartX=89.8 StartY=8 StartZ=0 EndX=18.3 EndY=8 EndZ=0
    g15: LineSegment StartX=18.3 StartY=8 StartZ=0 EndX=18.3 EndY=34.5 EndZ=0
    g16: Circle CenterX=7.5 CenterY=9 CenterZ=0 NormalX=0 NormalY=0 NormalZ=1 AngleXU=0 Radius=3.5
  constraints (47):
    c: Coincident(g0,g1)
    c: Coincident(g1,g2)
    c: Coincident(g2,g3)
    c: Coincident(g3,g0)
    c: Horizontal(g0)
    c: Horizontal(g2)
    c: Vertical(g1)
    c: Vertical(g3)
    c: DistanceX(g2,g1) = 80
    c: DistanceY(g1,g0) = 38.4
    c: DistanceX(g-1,g2) = 14
    c: DistanceY(g-1,g2) = 2
    c: Radius(g4) = 1.88
    c: Equal(g4,g5)
    c: Equal(g4,g6)
    c: Equal(g4,g7)
    c: Coincident(g8,g9)
    c: Coincident(g9,g10)
    c: Coincident(g10,g11)
    c: Coincident(g11,g8)
    c: Horizontal(g8)
    c: Horizontal(g10)
    c: Vertical(g9)
    c: Vertical(g11)
    c: DistanceX(g10,g9) = 75
    c: DistanceY(g9,g8) = 31.5
    c: Coincident(g8,g4)
    c: Coincident(g8,g5)
    c: Coincident(g9,g7)
    c: Coincident(g10,g6)
    c: DistanceX(g0,g4) = 2.5
    c: DistanceY(g4,g0) = 2.5
    c: Coincident(g12,g13)
    c: Coincident(g13,g14)
    c: Coincident(g14,g15)
    c: Coincident(g15,g12)
    c: Horizontal(g12)
    c: Horizontal(g14)
    c: Vertical(g13)
    c: Vertical(g15)
    c: DistanceY(g14,g12) = 26.5
    c: DistanceX(g14,g13) = 71.5
    c: DistanceY(g12,g0) = 5.9
    c: DistanceX(g2,g14) = 4.3
    c: DistanceY(g1,g16) = 7
    c: Radius(g16) = 3.5
    c: DistanceX(g16,g6) = 9
FEATURE [PartDesign::Pocket] Pocket012  label="Öffnung LCD 1602"
  BaseFeature = -> Pad011
  Length = 5
  Length2 = 100
  Placement = pos=(0,0,0) rot=(1,0,0;1.5708rad)
  Profile = -> Sketch017
  Reversed = true
  Type = 1
FEATURE [PartDesign::Plane] DatumPlane006
  Length = 123.344
  MapMode = 5
  Placement = pos=(0,0,0) rot=(-1,0,0;1.5708rad)
  ResizeMode = 0
  Support = -> [Pocket012]
  Width = 69.8441
FEATURE [PartDesign::Body] Body004  label="Front mit LCD 1602"
  Group = -> [Sketch016,Pad011,Sketch017,Pocket012,DatumPlane006]
  Origin = -> Origin004
  Placement = pos=(1,0,3) rot=(0,0,1;0rad)
  Tip = -> Pocket012
FEATURE [Sketcher::SketchObject] Sketch018
  MapMode = 5
  Placement = pos=(0,0,0) rot=(1,0,0;1.5708rad)
  Support = -> [XZ_Plane005]
  expr: Constraints[9] = Parameter.Breite - 2
  expr: Constraints[8] = 2 * Parameter.Hoehe - 2 * Parameter.Wandstaerke + 0.5
  sketch-geometry (4):
    g0: LineSegment StartX=0 StartY=44.5 StartZ=0 EndX=98 EndY=44.5 EndZ=0
    g1: LineSegment StartX=98 StartY=44.5 StartZ=0 EndX=98 EndY=0 EndZ=0
    g2: LineSegment StartX=98 StartY=0 StartZ=0 EndX=0 EndY=0 EndZ=0
    g3: LineSegment StartX=0 StartY=0 StartZ=0 EndX=0 EndY=44.5 EndZ=0
  constraints (11):
    c: Coincident(g0,g1)
    c: Coincident(g1,g2)
    c: Coincident(g2,g3)
    c: Coincident(g3,g0)
    c: Horizontal(g0)
    c: Horizontal(g2)
    c: Vertical(g1)
    c: Vertical(g3)
    c: DistanceY(g1,g0) = 44.5
    c: DistanceX(g2,g1) = 98
    c: Coincident(g-1,g2)
FEATURE [PartDesign::Pad] Pad012  label="Rückwand"
  Length = 2
  Length2 = 100
  Placement = pos=(0,0,0) rot=(1,0,0;1.5708rad)
  Profile = -> Sketch018
  Type = 0
FEATURE [PartDesign::Plane] DatumPlane007
  Length = 24
  MapMode = 5
  Placement = pos=(0,-2,-4e-16) rot=(1,0,0;1.5708rad)
  ResizeMode = 0
  Support = -> [Pad012]
  Width = 24
FEATURE [Sketcher::SketchObject] Sketch019
  MapMode = 5
  Placement = pos=(0,-2,-4e-16) rot=(1,0,0;1.5708rad)
  Support = -> [DatumPlane007]
  sketch-geometry (4):
    g0: LineSegment StartX=40 StartY=35 StartZ=0 EndX=58 EndY=35 EndZ=0
    g1: LineSegment StartX=58 StartY=35 StartZ=0 EndX=58 EndY=25 EndZ=0
    g2: LineSegment StartX=58 StartY=25 StartZ=0 EndX=40 EndY=25 EndZ=0
    g3: LineSegment StartX=40 StartY=25 StartZ=0 EndX=40 EndY=35 EndZ=0
  constraints (12):
    c: Coincident(g0,g1)
    c: Coincident(g1,g2)
    c: Coincident(g2,g3)
    c: Coincident(g3,g0)
    c: Horizontal(g0)
    c: Horizontal(g2)
    c: Vertical(g1)
    c: Vertical(g3)
    c: DistanceY(g1,g0) = 10
    c: DistanceX(g0,g0) = 18
    c: DistanceY(g-1,g2) = 25
    c: DistanceX(g-1,g2) = 40
FEATURE [PartDesign::Pocket] Pocket013  label="USB ESP"
  BaseFeature = -> Pad012
  Length = 5
  Length2 = 100
  Placement = pos=(0,0,0) rot=(1,0,0;1.5708rad)
  Profile = -> Sketch019
  Type = 1
FEATURE [Sketcher::SketchObject] Sketch020
  MapMode = 5
  Placement = pos=(0,-2,-4e-16) rot=(1,0,0;1.5708rad)
  Support = -> [DatumPlane007]
  sketch-geometry (11):
    g0: LineSegment StartX=6 StartY=39 StartZ=0 EndX=19 EndY=39 EndZ=0
    g1: LineSegment StartX=19 StartY=39 StartZ=0 EndX=19 EndY=22 EndZ=0
    g2: LineSegment StartX=19 StartY=22 StartZ=0 EndX=6 EndY=22 EndZ=0
    g3: LineSegment StartX=6 StartY=22 StartZ=0 EndX=6 EndY=39 EndZ=0
    g4: Circle CenterX=12.5 CenterY=12 CenterZ=0 NormalX=0 NormalY=0 NormalZ=1 AngleXU=0 Radius=1.88
    g5: LineSegment StartX=80 StartY=36 StartZ=0 EndX=92 EndY=36 EndZ=0
    g6: LineSegment StartX=92 StartY=36 StartZ=0 EndX=92 EndY=16 EndZ=0
    g7: LineSegment StartX=92 StartY=16 StartZ=0 EndX=80 EndY=16 EndZ=0
    g8: LineSegment StartX=80 StartY=16 StartZ=0 EndX=80 EndY=36 EndZ=0
    g9: Circle CenterX=86 CenterY=38.5 CenterZ=0 NormalX=0 NormalY=0 NormalZ=1 AngleXU=0 Radius=1.5
    g10: Circle CenterX=86 CenterY=13.5 CenterZ=0 NormalX=0 NormalY=0 NormalZ=1 AngleXU=0 Radius=1.5
  constraints (33):
    c: Coincident(g0,g1)
    c: Coincident(g1,g2)
    c: Coincident(g2,g3)
    c: Coincident(g3,g0)
    c: Horizontal(g0)
    c: Horizontal(g2)
    c: Vertical(g1)
    c: Vertical(g3)
    c: DistanceX(g2,g1) = 13
    c: DistanceY(g1,g0) = 17
    c: DistanceX(g-1,g0) = 6
    c: DistanceY(g-1,g2) = 22
    c: Radius(g4) = 1.88
    c: Coincident(g5,g6)
    c: Coincident(g6,g7)
    c: Coincident(g7,g8)
    c: Coincident(g8,g5)
    c: Horizontal(g5)
    c: Horizontal(g7)
    c: Vertical(g6)
    c: Vertical(g8)
    c: DistanceX(g7,g6) = 12
    c: DistanceY(g6,g5) = 20
    c: DistanceY(g5,g9) = 2.5
    c: DistanceY(g10,g7) = 2.5
    c: Radius(g9) = 1.5
    c: DistanceX(g7,g10) = 6
    c: DistanceX(g5,g9) = 6
    c: DistanceX(g-1,g7) = 80
    c: DistanceY(g-1,g7) = 16
    c: DistanceX(g2,g4) = 6.5
    c: DistanceY(g4,g2) = 10
    c: Equal(g9,g10)
FEATURE [PartDesign::Pocket] Pocket014  label="DHT11-SubD"
  BaseFeature = -> Pocket013
  Length = 5
  Length2 = 100
  Placement = pos=(0,0,0) rot=(1,0,0;1.5708rad)
  Profile = -> Sketch020
  Type = 1
FEATURE [PartDesign::Body] Body005  label="Rückseite - IoTSensor"
  Group = -> [Sketch018,Pad012,DatumPlane007,Sketch019,Pocket013,Sketch020,Pocket014]
  Origin = -> Origin005
  Tip = -> Pocket014
FEATURE [PartDesign::FeatureBase] BaseFeature001
  BaseFeature = -> Body
FEATURE [Sketcher::SketchObject] Sketch021
  MapMode = 5
  Placement = pos=(0,0,25) rot=(0,0,1;0rad)
  Support = -> [BaseFeature001]
  expr: Constraints[6] = Parameter.Helper_Abstand_Schalenverschraubung_Aussen
  expr: Constraints[5] = Parameter.Helper_Abstand_Schalenverschraubung_Aussen
  expr: Constraints[4] = Parameter.Tiefe / 2
  expr: Constraints[3] = Parameter.Breite
  expr: Constraints[0] = Parameter.Tiefe / 2
  sketch-geometry (3):
    g0: Circle CenterX=7 CenterY=60 CenterZ=0 NormalX=0 NormalY=0 NormalZ=1 AngleXU=0 Radius=4
    g1: Circle CenterX=93 CenterY=60 CenterZ=0 NormalX=0 NormalY=0 NormalZ=1 AngleXU=0 Radius=4
    g2: LineSegment [constr] StartX=0 StartY=0 StartZ=0 EndX=100 EndY=0 EndZ=0
  constraints (9):
    c: DistanceY(g-1,g0) = 60
    c: Coincident(g2,g-1)
    c: Horizontal(g2)
    c: DistanceX(g-1,g2) = 100
    c: DistanceY(g2,g1) = 60
    c: DistanceX(g-1,g0) = 7
    c: DistanceX(g1,g2) = 7
    c: Radius(g0) = 4
    c: Equal(g0,g1)
FEATURE [PartDesign::Pocket] Pocket015  label="Innenhalter"
  BaseFeature = -> BaseFeature001
  Length = 10
  Length2 = 100
  Profile = -> Sketch021
  Type = 0
FEATURE [Sketcher::SketchObject] Sketch022
  MapMode = 5
  Support = -> [XY_Plane006]
  expr: Constraints[6] = Parameter.Helper_Abstand_Schalenverschraubung_Aussen
  expr: Constraints[4] = Parameter.Tiefe / 2
  expr: Constraints[3] = Parameter.Tiefe / 2
  expr: Constraints[5] = Parameter.Helper_Abstand_Schalenverschraubung_Aussen
  expr: Constraints[2] = Parameter.Breite
  sketch-geometry (3):
    g0: Circle CenterX=7 CenterY=60 CenterZ=0 NormalX=0 NormalY=0 NormalZ=1 AngleXU=0 Radius=1.88
    g1: Circle CenterX=93 CenterY=60 CenterZ=0 NormalX=0 NormalY=0 NormalZ=1 AngleXU=0 Radius=1.88
    g2: LineSegment [constr] StartX=0 StartY=0 StartZ=0 EndX=100 EndY=0 EndZ=0
  constraints (9):
    c: Coincident(g2,g-1)
    c: PointOnObject(g2,g-1)
    c: DistanceX(g-1,g2) = 100
    c: DistanceY(g-1,g0) = 60
    c: DistanceY(g2,g1) = 60
    c: DistanceX(g-1,g0) = 7
    c: DistanceX(g1,g2) = 7
    c: Equal(g0,g1)
    c: Radius(g0) = 1.88
FEATURE [PartDesign::Pocket] Pocket016  label="Verschraubung Unterteil Oberteil"
  BaseFeature = -> Pocket015
  Length = 5
  Length2 = 100
  Profile = -> Sketch022
  Reversed = true
  Type = 1
FEATURE [Sketcher::SketchObject] Sketch023
  MapMode = 5
  Placement = pos=(0,0,0) rot=(1,0,0;3.14159rad)
  Support = -> [Pocket016]
  expr: Constraints[6] = Parameter.Breite
  expr: Constraints[4] = Parameter.Tiefe / 2
  expr: Constraints[3] = Parameter.Helper_Abstand_Schalenverschraubung_Aussen
  expr: Constraints[5] = Parameter.Tiefe / 2
  expr: Constraints[2] = Parameter.Helper_Abstand_Schalenverschraubung_Aussen
  sketch-geometry (3):
    g0: Circle CenterX=93 CenterY=-60 CenterZ=0 NormalX=0 NormalY=0 NormalZ=1 AngleXU=0 Radius=4
    g1: Circle CenterX=7 CenterY=-60 CenterZ=0 NormalX=0 NormalY=0 NormalZ=1 AngleXU=0 Radius=4
    g2: LineSegment [constr] StartX=0 StartY=0 StartZ=0 EndX=100 EndY=0 EndZ=0
  constraints (9):
    c: Coincident(g2,g-1)
    c: PointOnObject(g2,g-1)
    c: DistanceX(g-1,g1) = 7
    c: DistanceX(g0,g2) = 7
    c: DistanceY(g1,g-1) = 60
    c: DistanceY(g0,g2) = 60
    c: DistanceX(g-1,g2) = 100
    c: Equal(g1,g0)
    c: Radius(g1) = 4
FEATURE [PartDesign::Pocket] Pocket017  label="Schraubkopf Versenkung"
  BaseFeature = -> Pocket016
  Length = 3
  Length2 = 100
  Profile = -> Sketch023
  Type = 0
FEATURE [Sketcher::SketchObject] Sketch024
  MapMode = 5
  Placement = pos=(0,0,0) rot=(1,0,0;3.14159rad)
  Support = -> [Pocket017]
  expr: Constraints[82] = Parameter.Tiefe
  expr: Constraints[65] = Parameter.Luftschlitz_Breite_Boden
  expr: Constraints[64] = Parameter.Luftschlitz_Tiefe_Boden
  expr: Constraints[9] = Parameter.Breite
  sketch-geometry (28):
    g0: LineSegment [constr] StartX=0 StartY=0 StartZ=0 EndX=100 EndY=0 EndZ=0
    g1: LineSegment [constr] StartX=100 StartY=0 StartZ=0 EndX=100 EndY=-120 EndZ=0
    g2: LineSegment [constr] StartX=100 StartY=-120 StartZ=0 EndX=0 EndY=-120 EndZ=0
    g3: LineSegment [constr] StartX=0 StartY=-120 StartZ=0 EndX=0 EndY=0 EndZ=0
    g4: LineSegment StartX=100 StartY=-31 StartZ=0 EndX=70 EndY=-31 EndZ=0
    g5: LineSegment StartX=70 StartY=-31 StartZ=0 EndX=70 EndY=-34 EndZ=0
    g6: LineSegment StartX=70 StartY=-34 StartZ=0 EndX=100 EndY=-34 EndZ=0
    g7: LineSegment StartX=100 StartY=-34 StartZ=0 EndX=100 EndY=-31 EndZ=0
    g8: LineSegment StartX=100 StartY=-37 StartZ=0 EndX=70 EndY=-37 EndZ=0
    g9: LineSegment StartX=70 StartY=-37 StartZ=0 EndX=70 EndY=-40 EndZ=0
    g10: LineSegment StartX=70 StartY=-40 StartZ=0 EndX=100 EndY=-40 EndZ=0
    g11: LineSegment StartX=100 StartY=-40 StartZ=0 EndX=100 EndY=-37 EndZ=0
    g12: LineSegment StartX=100 StartY=-25 StartZ=0 EndX=70 EndY=-25 EndZ=0
    g13: LineSegment StartX=70 StartY=-25 StartZ=0 EndX=70 EndY=-28 EndZ=0
    g14: LineSegment StartX=70 StartY=-28 StartZ=0 EndX=100 EndY=-28 EndZ=0
    g15: LineSegment StartX=100 StartY=-28 StartZ=0 EndX=100 EndY=-25 EndZ=0
    g16: LineSegment StartX=0 StartY=-25 StartZ=0 EndX=30 EndY=-25 EndZ=0
    g17: LineSegment StartX=30 StartY=-25 StartZ=0 EndX=30 EndY=-28 EndZ=0
    g18: LineSegment StartX=30 StartY=-28 StartZ=0 EndX=0 EndY=-28 EndZ=0
    g19: LineSegment StartX=0 StartY=-28 StartZ=0 EndX=0 EndY=-25 EndZ=0
    g20: LineSegment StartX=0 StartY=-31 StartZ=0 EndX=30 EndY=-31 EndZ=0
    g21: LineSegment StartX=30 StartY=-31 StartZ=0 EndX=30 EndY=-34 EndZ=0
    g22: LineSegment StartX=30 StartY=-34 StartZ=0 EndX=0 EndY=-34 EndZ=0
    g23: LineSegment StartX=0 StartY=-34 StartZ=0 EndX=0 EndY=-31 EndZ=0
    g24: LineSegment StartX=0 StartY=-37 StartZ=0 EndX=30 EndY=-37 EndZ=0
    g25: LineSegment StartX=30 StartY=-37 StartZ=0 EndX=30 EndY=-40 EndZ=0
    g26: LineSegment StartX=30 StartY=-40 StartZ=0 EndX=0 EndY=-40 EndZ=0
    g27: LineSegment StartX=0 StartY=-40 StartZ=0 EndX=0 EndY=-37 EndZ=0
  constraints (83):
    c: Coincident(g0,g1)
    c: Coincident(g1,g2)
    c: Coincident(g2,g3)
    c: Coincident(g3,g0)
    c: Horizontal(g0)
    c: Horizontal(g2)
    c: Vertical(g1)
    c: Vertical(g3)
    c: Coincident(g0,g-1)
    c: DistanceX(g-1,g0) = 100
    c: Coincident(g4,g5)
    c: Coincident(g5,g6)
    c: Coincident(g6,g7)
    c: Coincident(g7,g4)
    c: Horizontal(g4)
    c: Horizontal(g6)
    c: Vertical(g5)
    c: Vertical(g7)
    c: PointOnObject(g4,g1)
    c: Coincident(g8,g9)
    c: Coincident(g9,g10)
    c: Coincident(g10,g11)
    c: Coincident(g11,g8)
    c: Horizontal(g8)
    c: Horizontal(g10)
    c: Vertical(g9)
    c: Vertical(g11)
    c: PointOnObject(g8,g1)
    c: Coincident(g12,g13)
    c: Coincident(g13,g14)
    c: Coincident(g14,g15)
    c: Coincident(g15,g12)
    c: Horizontal(g12)
    c: Horizontal(g14)
    c: Vertical(g13)
    c: Vertical(g15)
    c: PointOnObject(g12,g1)
    c: Coincident(g16,g17)
    c: Coincident(g17,g18)
    c: Coincident(g18,g19)
    c: Coincident(g19,g16)
    c: Horizontal(g16)
    c: Horizontal(g18)
    c: Vertical(g17)
    c: Vertical(g19)
    c: PointOnObject(g16,g3)
    c: Coincident(g20,g21)
    c: Coincident(g21,g22)
    c: Coincident(g22,g23)
    c: Coincident(g23,g20)
    c: Horizontal(g20)
    c: Horizontal(g22)
    c: Vertical(g21)
    c: Vertical(g23)
    c: PointOnObject(g20,g3)
    c: Coincident(g24,g25)
    c: Coincident(g25,g26)
    c: Coincident(g26,g27)
    c: Coincident(g27,g24)
    c: Horizontal(g24)
    c: Horizontal(g26)
    c: Vertical(g25)
    c: Vertical(g27)
    c: PointOnObject(g24,g3)
    c: DistanceY(g17,g16) = 3
    c: DistanceX(g16,g16) = 30
    c: Equal(g16,g12)
    c: Equal(g12,g20)
    c: Equal(g20,g4)
    c: Equal(g4,g24)
    c: Equal(g24,g8)
    c: Equal(g17,g13)
    c: Equal(g17,g21)
    c: Equal(g21,g5)
    c: Equal(g5,g25)
    c: Equal(g25,g9)
    c: DistanceY(g20,g17) = 3
    c: DistanceY(g24,g21) = 3
    c: DistanceY(g4,g13) = 3
    c: DistanceY(g8,g5) = 3
    c: DistanceY(g12,g0) = 25
    c: DistanceY(g16,g-1) = 25
    c: DistanceY(g1,g0) = 120
FEATURE [PartDesign::Pocket] Pocket018  label="Lüftungsschlitze Oberschale"
  BaseFeature = -> Pocket017
  Length = 10
  Length2 = 100
  Profile = -> Sketch024
  Type = 0
FEATURE [Sketcher::SketchObject] Sketch025
  MapMode = 5
  Placement = pos=(0,0,25) rot=(0,0,1;0rad)
  Support = -> [Pocket018]
  expr: Constraints[6] = Parameter.Nut_Feder_Entfernung_Vorne_Hinten
  expr: Constraints[28] = Parameter.Nut_Feder_Breite
  expr: Constraints[31] = (Parameter.Wandstaerke - Parameter.Nut_Feder_Breite) / 2
  expr: Constraints[30] = (Parameter.Wandstaerke - Parameter.Nut_Feder_Breite) / 2
  expr: Constraints[7] = Parameter.Tiefe - 2 * Parameter.Nut_Feder_Entfernung_Vorne_Hinten
  expr: Constraints[4] = Parameter.Breite
  sketch-geometry (10):
    g0: LineSegment [constr] StartX=0 StartY=110 StartZ=0 EndX=100 EndY=110 EndZ=0
    g1: LineSegment [constr] StartX=0 StartY=10 StartZ=0 EndX=100 EndY=10 EndZ=0
    g2: LineSegment StartX=1 StartY=110 StartZ=0 EndX=2 EndY=110 EndZ=0
    g3: LineSegment StartX=2 StartY=110 StartZ=0 EndX=2 EndY=10 EndZ=0
    g4: LineSegment StartX=2 StartY=10 StartZ=0 EndX=1 EndY=10 EndZ=0
    g5: LineSegment StartX=1 StartY=10 StartZ=0 EndX=1 EndY=110 EndZ=0
    g6: LineSegment StartX=98 StartY=110 StartZ=0 EndX=99 EndY=110 EndZ=0
    g7: LineSegment StartX=99 StartY=110 StartZ=0 EndX=99 EndY=10 EndZ=0
    g8: LineSegment StartX=99 StartY=10 StartZ=0 EndX=98 EndY=10 EndZ=0
    g9: LineSegment StartX=98 StartY=10 StartZ=0 EndX=98 EndY=110 EndZ=0
  constraints (32):
    c: PointOnObject(g0,g-2)
    c: Horizontal(g0)
    c: PointOnObject(g1,g-2)
    c: Horizontal(g1)
    c: DistanceX(g1,g1) = 100
    c: Equal(g1,g0)
    c: DistanceY(g-1,g1) = 10
    c: DistanceY(g1,g0) = 100
    c: Coincident(g2,g3)
    c: Coincident(g3,g4)
    c: Coincident(g4,g5)
    c: Coincident(g5,g2)
    c: Horizontal(g2)
    c: Horizontal(g4)
    c: Vertical(g3)
    c: Vertical(g5)
    c: PointOnObject(g2,g0)
    c: PointOnObject(g3,g1)
    c: Coincident(g6,g7)
    c: Coincident(g7,g8)
    c: Coincident(g8,g9)
    c: Coincident(g9,g6)
    c: Horizontal(g6)
    c: Horizontal(g8)
    c: Vertical(g7)
    c: Vertical(g9)
    c: PointOnObject(g6,g0)
    c: PointOnObject(g7,g1)
    c: DistanceX(g2,g2) = 1
    c: Equal(g2,g6)
    c: DistanceX(g0,g2) = 1
    c: DistanceX(g6,g0) = 1
FEATURE [PartDesign::Pocket] Pocket019  label="Nut Ober- Unterteil"
  BaseFeature = -> Pocket018
  Length = 3
  Length2 = 100
  Profile = -> Sketch025
  Type = 0
FEATURE [Sketcher::SketchObject] Sketch028
  MapMode = 5
  Placement = pos=(0,0,3) rot=(0,0,1;0rad)
  Support = -> [Pocket019]
  expr: Constraints[11] = (Parameter.Tiefe - 100) / 2
  expr: Constraints[10] = (Parameter.Breite - 70) / 2
  expr: Constraints[9] = Parameter.Tiefe - 20
  expr: Constraints[8] = Parameter.Breite - 30
  sketch-geometry (4):
    g0: LineSegment StartX=15 StartY=110 StartZ=0 EndX=85 EndY=110 EndZ=0
    g1: LineSegment StartX=85 StartY=110 StartZ=0 EndX=85 EndY=10 EndZ=0
    g2: LineSegment StartX=85 StartY=10 StartZ=0 EndX=15 EndY=10 EndZ=0
    g3: LineSegment StartX=15 StartY=10 StartZ=0 EndX=15 EndY=110 EndZ=0
  constraints (12):
    c: Coincident(g0,g1)
    c: Coincident(g1,g2)
    c: Coincident(g2,g3)
    c: Coincident(g3,g0)
    c: Horizontal(g0)
    c: Horizontal(g2)
    c: Vertical(g1)
    c: Vertical(g3)
    c: DistanceX(g2,g1) = 70
    c: DistanceY(g2,g0) = 100
    c: DistanceX(g-1,g2) = 15
    c: DistanceY(g-1,g2) = 10
FEATURE [PartDesign::Pocket] Pocket021
  BaseFeature = -> Pocket019
  Length = 2
  Length2 = 100
  Profile = -> Sketch028
  Type = 0
FEATURE [PartDesign::Body] Body006  label="Oberschale"
  BaseFeature = -> Body
  Group = -> [BaseFeature001,Sketch021,Pocket015,Sketch022,Pocket016,Sketch023,Pocket017,Sketch024,Pocket018,Sketch025,Pocket019,Sketch028,Pocket021]
  Origin = -> Origin006
  Tip = -> Pocket021
FEATURE [Sketcher::SketchObject] Sketch029
  MapMode = 5
  Support = -> [XY_Plane007]
  sketch-geometry (4):
    g0: LineSegment StartX=0 StartY=0 StartZ=0 EndX=60 EndY=0 EndZ=0
    g1: LineSegment StartX=60 StartY=0 StartZ=0 EndX=60 EndY=100 EndZ=0
    g2: LineSegment StartX=60 StartY=100 StartZ=0 EndX=0 EndY=100 EndZ=0
    g3: LineSegment StartX=0 StartY=100 StartZ=0 EndX=0 EndY=0 EndZ=0
  constraints (11):
    c: Coincident(g0,g1)
    c: Coincident(g1,g2)
    c: Coincident(g2,g3)
    c: Coincident(g3,g0)
    c: Horizontal(g0)
    c: Horizontal(g2)
    c: Vertical(g1)
    c: Vertical(g3)
    c: Coincident(g0,g-1)
    c: DistanceX(g0,g0) = 60
    c: DistanceY(g0,g2) = 100
FEATURE [PartDesign::Pad] Pad014  label="Grundplatte001"
  Length = 15
  Length2 = 100
  Profile = -> Sketch029
  Type = 0
FEATURE [Sketcher::SketchObject] Sketch031
  MapMode = 5
  Placement = pos=(0,0,15) rot=(0,0,1;0rad)
  Support = -> [Pad014]
  expr: Constraints[9] = Parameter.Platine_Tiefe - 2 * Parameter.Platine_Abstand_Bohrloch_Aussenrand
  expr: Constraints[8] = Parameter.Platine_Breite - 2 * Parameter.Platine_Abstand_Bohrloch_Aussenrand
  sketch-geometry (8):
    g0: LineSegment [constr] StartX=10 StartY=95 StartZ=0 EndX=50 EndY=95 EndZ=0
    g1: LineSegment [constr] StartX=50 StartY=95 StartZ=0 EndX=50 EndY=5 EndZ=0
    g2: LineSegment [constr] StartX=50 StartY=5 StartZ=0 EndX=10 EndY=5 EndZ=0
    g3: LineSegment [constr] StartX=10 StartY=5 StartZ=0 EndX=10 EndY=95 EndZ=0
    g4: Circle CenterX=10 CenterY=95 CenterZ=0 NormalX=0 NormalY=0 NormalZ=1 AngleXU=0 Radius=5
    g5: Circle CenterX=50 CenterY=95 CenterZ=0 NormalX=0 NormalY=0 NormalZ=1 AngleXU=0 Radius=5
    g6: Circle CenterX=50 CenterY=5 CenterZ=0 NormalX=0 NormalY=0 NormalZ=1 AngleXU=0 Radius=5
    g7: Circle CenterX=10 CenterY=5 CenterZ=0 NormalX=0 NormalY=0 NormalZ=1 AngleXU=0 Radius=5
  constraints (20):
    c: Coincident(g0,g1)
    c: Coincident(g1,g2)
    c: Coincident(g2,g3)
    c: Coincident(g3,g0)
    c: Horizontal(g0)
    c: Horizontal(g2)
    c: Vertical(g1)
    c: Vertical(g3)
    c: DistanceX(g2,g1) = 40
    c: DistanceY(g2,g0) = 90
    c: DistanceX(g-1,g2) = 10
    c: DistanceY(g-1,g2) = 5
    c: Coincident(g4,g0)
    c: Coincident(g5,g0)
    c: Coincident(g6,g1)
    c: Equal(g4,g5)
    c: Equal(g4,g6)
    c: Radius(g4) = 5
    c: Coincident(g7,g2)
    c: Equal(g6,g7)
FEATURE [PartDesign::Pocket] Pocket022  label="Befestigung"
  BaseFeature = -> Pad014
  Length = 4
  Length2 = 100
  Profile = -> Sketch031
  Type = 0
FEATURE [Sketcher::SketchObject] Sketch032
  MapMode = 5
  Placement = pos=(0,0,0) rot=(1,0,0;1.5708rad)
  Support = -> [XZ_Plane007]
  sketch-geometry (4):
    g0: LineSegment StartX=6 StartY=0 StartZ=0 EndX=54 EndY=0 EndZ=0
    g1: LineSegment StartX=54 StartY=0 StartZ=0 EndX=54 EndY=10 EndZ=0
    g2: LineSegment StartX=54 StartY=10 StartZ=0 EndX=6 EndY=10 EndZ=0
    g3: LineSegment StartX=6 StartY=10 StartZ=0 EndX=6 EndY=0 EndZ=0
  constraints (12):
    c: Coincident(g0,g1)
    c: Coincident(g1,g2)
    c: Coincident(g2,g3)
    c: Coincident(g3,g0)
    c: Horizontal(g0)
    c: Horizontal(g2)
    c: Vertical(g1)
    c: Vertical(g3)
    c: PointOnObject(g0,g-1)
    c: DistanceX(g0,g0) = 48
    c: DistanceX(g-1,g0) = 6
    c: DistanceY(g0,g1) = 10
FEATURE [PartDesign::Pocket] Pocket023  label="Einschub Frontal"
  BaseFeature = -> Pocket022
  Length = 5
  Length2 = 100
  Profile = -> Sketch032
  Type = 1
FEATURE [Sketcher::SketchObject] Sketch033
  MapMode = 5
  Placement = pos=(0,0,0) rot=(1,0,0;1.5708rad)
  Support = -> [Pocket023]
  sketch-geometry (14):
    g0: LineSegment [constr] StartX=4.5 StartY=3 StartZ=0 EndX=55.5 EndY=3 EndZ=0
    g1: LineSegment [constr] StartX=55.5 StartY=3 StartZ=0 EndX=55.5 EndY=1 EndZ=0
    g2: LineSegment [constr] StartX=55.5 StartY=1 StartZ=0 EndX=4.5 EndY=1 EndZ=0
    g3: LineSegment [constr] StartX=4.5 StartY=1 StartZ=0 EndX=4.5 EndY=3 EndZ=0
    g4: GeomPoint X=4.5 Y=1 Z=0
    g5: GeomPoint X=4.5 Y=1 Z=0
    g6: LineSegment StartX=4.5 StartY=3 StartZ=0 EndX=6 EndY=3 EndZ=0
    g7: LineSegment StartX=6 StartY=3 StartZ=0 EndX=6 EndY=1 EndZ=0
    g8: LineSegment StartX=6 StartY=1 StartZ=0 EndX=4.5 EndY=1 EndZ=0
    g9: LineSegment StartX=4.5 StartY=1 StartZ=0 EndX=4.5 EndY=3 EndZ=0
    g10: LineSegment StartX=55.5 StartY=3 StartZ=0 EndX=54 EndY=3 EndZ=0
    g11: LineSegment StartX=54 StartY=3 StartZ=0 EndX=54 EndY=1 EndZ=0
    g12: LineSegment StartX=54 StartY=1 StartZ=0 EndX=55.5 EndY=1 EndZ=0
    g13: LineSegment StartX=55.5 StartY=1 StartZ=0 EndX=55.5 EndY=3 EndZ=0
  constraints (36):
    c: Coincident(g0,g1)
    c: Coincident(g1,g2)
    c: Coincident(g2,g3)
    c: Coincident(g3,g0)
    c: Horizontal(g0)
    c: Vertical(g1)
    c: Vertical(g3)
    c: DistanceX(g-1,g2) = 4.5
    c: DistanceY(g2,g0) = 2
    c: DistanceY(g-1,g2) = 1
    c: Coincident(g4,g2)
    c: Coincident(g5,g4)
    c: Horizontal(g2)
    c: DistanceX(g4,g1) = 51
    c: Coincident(g6,g7)
    c: Coincident(g7,g8)
    c: Coincident(g8,g9)
    c: Coincident(g9,g6)
    c: Horizontal(g6)
    c: Horizontal(g8)
    c: Vertical(g7)
    c: Vertical(g9)
    c: Coincident(g6,g0)
    c: PointOnObject(g7,g2)
    c: DistanceX(g6,g6) = 1.5
    c: Coincident(g10,g11)
    c: Coincident(g11,g12)
    c: Coincident(g12,g13)
    c: Coincident(g13,g10)
    c: Horizontal(g10)
    c: Horizontal(g12)
    c: Vertical(g11)
    c: Vertical(g13)
    c: Coincident(g10,g0)
    c: PointOnObject(g11,g2)
    c: Equal(g6,g10)
FEATURE [PartDesign::Pocket] Pocket024  label="Einschübe"
  BaseFeature = -> Pocket023
  Length = 5
  Length2 = 100
  Profile = -> Sketch033
  Type = 1
FEATURE [Sketcher::SketchObject] Sketch034
  MapMode = 5
  Placement = pos=(0,2.2e-15,10) rot=(1,0,0;3.14159rad)
  Support = -> [Pocket024]
  sketch-geometry (4):
    g0: LineSegment StartX=6 StartY=-14 StartZ=0 EndX=54 EndY=-14 EndZ=0
    g1: LineSegment StartX=54 StartY=-14 StartZ=0 EndX=54 EndY=-86 EndZ=0
    g2: LineSegment StartX=54 StartY=-86 StartZ=0 EndX=6 EndY=-86 EndZ=0
    g3: LineSegment StartX=6 StartY=-86 StartZ=0 EndX=6 EndY=-14 EndZ=0
  constraints (12):
    c: Coincident(g0,g1)
    c: Coincident(g1,g2)
    c: Coincident(g2,g3)
    c: Coincident(g3,g0)
    c: Horizontal(g0)
    c: Horizontal(g2)
    c: Vertical(g1)
    c: Vertical(g3)
    c: DistanceX(g0,g0) = 48
    c: DistanceX(g-1,g0) = 6
    c: DistanceY(g1,g0) = 72
    c: DistanceY(g0,g-1) = 14
FEATURE [PartDesign::Pocket] Pocket025  label="Leerraum"
  BaseFeature = -> Pocket024
  Length = 5
  Length2 = 100
  Profile = -> Sketch034
  Type = 1
FEATURE [Sketcher::SketchObject] Sketch035
  MapMode = 5
  Support = -> [XY_Plane007]
  expr: Constraints[9] = Parameter.Platine_Tiefe - 2 * Parameter.Platine_Abstand_Bohrloch_Aussenrand
  expr: Constraints[8] = Parameter.Platine_Breite - 2 * Parameter.Platine_Abstand_Bohrloch_Aussenrand
  sketch-geometry (8):
    g0: LineSegment [constr] StartX=10 StartY=95 StartZ=0 EndX=50 EndY=95 EndZ=0
    g1: LineSegment [constr] StartX=50 StartY=95 StartZ=0 EndX=50 EndY=5 EndZ=0
    g2: LineSegment [constr] StartX=50 StartY=5 StartZ=0 EndX=10 EndY=5 EndZ=0
    g3: LineSegment [constr] StartX=10 StartY=5 StartZ=0 EndX=10 EndY=95 EndZ=0
    g4: Circle CenterX=10 CenterY=95 CenterZ=0 NormalX=0 NormalY=0 NormalZ=1 AngleXU=0 Radius=1.88
    g5: Circle CenterX=50 CenterY=95 CenterZ=0 NormalX=0 NormalY=0 NormalZ=1 AngleXU=0 Radius=1.88
    g6: Circle CenterX=10 CenterY=5 CenterZ=0 NormalX=0 NormalY=0 NormalZ=1 AngleXU=0 Radius=1.88
    g7: Circle CenterX=50 CenterY=5 CenterZ=0 NormalX=0 NormalY=0 NormalZ=1 AngleXU=0 Radius=1.88
  constraints (20):
    c: Coincident(g0,g1)
    c: Coincident(g1,g2)
    c: Coincident(g2,g3)
    c: Coincident(g3,g0)
    c: Horizontal(g0)
    c: Horizontal(g2)
    c: Vertical(g1)
    c: Vertical(g3)
    c: DistanceX(g0,g0) = 40
    c: DistanceY(g1,g0) = 90
    c: DistanceX(g-1,g2) = 10
    c: DistanceY(g-1,g2) = 5
    c: Coincident(g4,g0)
    c: Coincident(g5,g0)
    c: Coincident(g6,g2)
    c: Coincident(g7,g1)
    c: Equal(g4,g5)
    c: Equal(g4,g6)
    c: Equal(g4,g7)
    c: Radius(g4) = 1.88
FEATURE [Sketcher::SketchObject] Sketch036
  MapMode = 5
  Support = -> [XY_Plane008]
  expr: Constraints[10] = Parameter.Breite - 2
  expr: Constraints[9] = 2 * Parameter.Hoehe - 2 * Parameter.Wandstaerke + 0.5
  sketch-geometry (12):
    g0: LineSegment StartX=0 StartY=0 StartZ=0 EndX=98 EndY=0 EndZ=0
    g1: LineSegment StartX=98 StartY=0 StartZ=0 EndX=98 EndY=44.5 EndZ=0
    g2: LineSegment StartX=98 StartY=44.5 StartZ=0 EndX=0 EndY=44.5 EndZ=0
    g3: LineSegment StartX=0 StartY=44.5 StartZ=0 EndX=0 EndY=0 EndZ=0
    g4: Circle CenterX=10 CenterY=10 CenterZ=0 NormalX=0 NormalY=0 NormalZ=1 AngleXU=0 Radius=4
    g5: Circle CenterX=10 CenterY=25 CenterZ=0 NormalX=0 NormalY=0 NormalZ=1 AngleXU=0 Radius=2.5
    g6: LineSegment StartX=83 StartY=32.5 StartZ=0 EndX=95 EndY=32.5 EndZ=0
    g7: LineSegment StartX=95 StartY=32.5 StartZ=0 EndX=95 EndY=12.5 EndZ=0
    g8: LineSegment StartX=95 StartY=12.5 StartZ=0 EndX=83 EndY=12.5 EndZ=0
    g9: LineSegment StartX=83 StartY=12.5 StartZ=0 EndX=83 EndY=32.5 EndZ=0
    g10: Circle CenterX=89 CenterY=35 CenterZ=0 NormalX=0 NormalY=0 NormalZ=1 AngleXU=0 Radius=1.5
    g11: Circle CenterX=89 CenterY=10 CenterZ=0 NormalX=0 NormalY=0 NormalZ=1 AngleXU=0 Radius=1.5
  constraints (35):
    c: Coincident(g0,g1)
    c: Coincident(g1,g2)
    c: Coincident(g2,g3)
    c: Coincident(g3,g0)
    c: Horizontal(g0)
    c: Horizontal(g2)
    c: Vertical(g1)
    c: Vertical(g3)
    c: Coincident(g0,g-1)
    c: DistanceY(g0,g1) = 44.5
    c: DistanceX(g0,g0) = 98
    c: DistanceX(g0,g4) = 10
    c: Radius(g4) = 4
    c: Radius(g5) = 2.5
    c: DistanceX(g2,g5) = 10
    c: DistanceY(g4,g5) = 15
    c: DistanceY(g0,g4) = 10
    c: Coincident(g6,g7)
    c: Coincident(g7,g8)
    c: Coincident(g8,g9)
    c: Coincident(g9,g6)
    c: Horizontal(g6)
    c: Horizontal(g8)
    c: Vertical(g7)
    c: Vertical(g9)
    c: DistanceX(g6,g6) = 12
    c: DistanceY(g8,g6) = 20
    c: Equal(g10,g11)
    c: Radius(g10) = 1.5
    c: DistanceX(g6,g10) = 6
    c: DistanceX(g8,g11) = 6
    c: DistanceY(g11,g7) = 2.5
    c: DistanceY(g6,g10) = 2.5
    c: DistanceY(g0,g7) = 12.5
    c: DistanceX(g7,g0) = 3
FEATURE [PartDesign::Pad] Pad015  label="Grundplatte002"
  Length = 2
  Length2 = 100
  Profile = -> Sketch036
  Type = 0
FEATURE [PartDesign::Body] Body008  label="Rückseite - Magloop"
  Group = -> [Sketch036,Pad015]
  Origin = -> Origin008
  Tip = -> Pad015
FEATURE [PartDesign::Pocket] Pocket026
  BaseFeature = -> Pocket025
  Length = 5
  Length2 = 100
  Profile = -> Sketch035
  Reversed = true
  Type = 1
FEATURE [PartDesign::Body] Body007  label="Halter für Platinen 100x50m"
  Group = -> [Sketch029,Pad014,Sketch031,Pocket022,Sketch032,Pocket023,Sketch033,Pocket024,Sketch034,Pocket025,Sketch035,Pocket026]
  Origin = -> Origin007
  Tip = -> Pocket026
FEATURE [PartDesign::Body] Body003  label="Unterseite"
  BaseFeature = -> Body
  Group = -> [BaseFeature,Pad009,Sketch007,DatumPlane002,Sketch010,Pocket006,DatumPlane003,Pad010,Sketch011,DatumPlane004,Sketch012,Pocket007,DatumPlane005,Sketch013,Pocket008,Sketch014,Pocket009,Sketch015,Pocket010,Fillet,Sketch026,Pad013,Sketch027,Pocket020]
  Origin = -> Origin003
  Tip = -> Pocket020
FEATURE [Sketcher::SketchObject] Sketch011
  MapMode = 5
  Placement = pos=(0,0,25) rot=(0,0,1;0rad)
  Support = -> [Pocket010]
  expr: Constraints[16] = Parameter.Tiefe / 2
  expr: Constraints[15] = Parameter.Helper_Abstand_Schalenverschraubung_Aussen
  expr: Constraints[10] = Parameter.Tiefe
  expr: Constraints[14] = Parameter.Helper_Abstand_Schalenverschraubung_Aussen
  expr: Constraints[9] = Parameter.Breite
  sketch-geometry (7):
    g0: Circle CenterX=7 CenterY=60 CenterZ=0 NormalX=0 NormalY=0 NormalZ=1 AngleXU=0 Radius=4
    g1: Circle CenterX=93 CenterY=60 CenterZ=0 NormalX=0 NormalY=0 NormalZ=1 AngleXU=0 Radius=4
    g2: LineSegment [constr] StartX=0 StartY=120 StartZ=0 EndX=100 EndY=120 EndZ=0
    g3: LineSegment [constr] StartX=100 StartY=120 StartZ=0 EndX=100 EndY=0 EndZ=0
    g4: LineSegment [constr] StartX=100 StartY=0 StartZ=0 EndX=0 EndY=0 EndZ=0
    g5: LineSegment [constr] StartX=0 StartY=0 StartZ=0 EndX=0 EndY=120 EndZ=0
    g6: LineSegment [constr] StartX=7 StartY=60 StartZ=0 EndX=93 EndY=60 EndZ=0
  constraints (19):
    c: Coincident(g2,g3)
    c: Coincident(g3,g4)
    c: Coincident(g4,g5)
    c: Coincident(g5,g2)
    c: Horizontal(g2)
    c: Horizontal(g4)
    c: Vertical(g3)
    c: Vertical(g5)
    c: Coincident(g-1,g4)
    c: DistanceX(g-1,g3) = 100
    c: DistanceY(g-1,g2) = 120
    c: Radius(g0) = 4
    c: Equal(g0,g1)
    c: Horizontal(g6)
    c: DistanceX(g6,g3) = 7
    c: DistanceX(g-1,g6) = 7
    c: DistanceY(g-1,g6) = 60
    c: Coincident(g6,g0)
    c: Coincident(g1,g6)
FEATURE [PartDesign::Pocket] Pocket007  label="Verschraubung Ober- und Unterteil"
  BaseFeature = -> Pad010
  Length = 5
  Length2 = 100
  Profile = -> Sketch012
  Type = 1
FEATURE [PartDesign::Plane] DatumPlane005  label="Ebene Unterseite"
  Length = 133.917
  MapMode = 5
  Placement = pos=(0,0,0) rot=(1,0,0;3.14159rad)
  ResizeMode = 0
  Support = -> [Pocket007]
  Width = 153.917
FEATURE [Sketcher::SketchObject] Sketch013
  MapMode = 5
  Placement = pos=(0,0,0) rot=(1,0,0;3.14159rad)
  Support = -> [DatumPlane005]
  expr: Constraints[21] = Parameter.Platine_Tiefe - 2 * Parameter.Platine_Abstand_Bohrloch_Aussenrand
  expr: Constraints[14] = Parameter.Breite
  expr: Constraints[17] = Parameter.Helper_Abstand_Schalenverschraubung_Aussen
  expr: Constraints[22] = (Parameter.Breite - (Parameter.Platine_Breite - 2 * Parameter.Platine_Abstand_Bohrloch_Aussenrand)) / 2
  expr: Constraints[15] = Parameter.Tiefe
  expr: Constraints[20] = Parameter.Platine_Breite - 2 * Parameter.Platine_Abstand_Bohrloch_Aussenrand
  expr: Constraints[18] = Parameter.Tiefe / 2
  expr: Constraints[16] = Parameter.Helper_Abstand_Schalenverschraubung_Aussen
  sketch-geometry (13):
    g0: LineSegment [constr] StartX=30 StartY=-12 StartZ=0 EndX=70 EndY=-12 EndZ=0
    g1: LineSegment [constr] StartX=70 StartY=-12 StartZ=0 EndX=70 EndY=-102 EndZ=0
    g2: LineSegment [constr] StartX=70 StartY=-102 StartZ=0 EndX=30 EndY=-102 EndZ=0
    g3: LineSegment [constr] StartX=30 StartY=-102 StartZ=0 EndX=30 EndY=-12 EndZ=0
    g4: LineSegment [constr] StartX=7 StartY=-60 StartZ=0 EndX=93 EndY=-60 EndZ=0
    g5: LineSegment [constr] StartX=0 StartY=0 StartZ=0 EndX=100 EndY=0 EndZ=0
    g6: LineSegment [constr] StartX=100 StartY=0 StartZ=0 EndX=100 EndY=-120 EndZ=0
    g7: LineSegment [constr] StartX=100 StartY=-120 StartZ=0 EndX=0 EndY=-120 EndZ=0
    g8: LineSegment [constr] StartX=0 StartY=-120 StartZ=0 EndX=0 EndY=0 EndZ=0
    g9: Circle CenterX=30 CenterY=-102 CenterZ=0 NormalX=0 NormalY=0 NormalZ=1 AngleXU=0 Radius=3
    g10: Circle CenterX=70 CenterY=-102 CenterZ=0 NormalX=0 NormalY=0 NormalZ=1 AngleXU=0 Radius=3
    g11: Circle CenterX=30 CenterY=-12 CenterZ=0 NormalX=0 NormalY=0 NormalZ=1 AngleXU=0 Radius=3
    g12: Circle CenterX=70 CenterY=-12 CenterZ=0 NormalX=0 NormalY=0 NormalZ=1 AngleXU=0 Radius=3
  constraints (35):
    c: Horizontal(g0)
    c: Horizontal(g2)
    c: Vertical(g1)
    c: Vertical(g3)
    c: Horizontal(g4)
    c: Coincident(g5,g6)
    c: Coincident(g6,g7)
    c: Coincident(g7,g8)
    c: Coincident(g8,g5)
    c: Horizontal(g5)
    c: Horizontal(g7)
    c: Vertical(g6)
    c: Vertical(g8)
    c: Coincident(g-1,g5)
    c: DistanceX(g-1,g5) = 100
    c: DistanceY(g7,g-1) = 120
    c: DistanceX(g7,g4) = 7
    c: DistanceX(g4,g6) = 7
    c: DistanceY(g7,g4) = 60
    c: DistanceY(g0,g-1) = 12
    c: DistanceX(g0,g0) = 40
    c: DistanceY(g1,g0) = 90
    c: DistanceX(g-1,g0) = 30
    c: Coincident(g0,g11)
    c: Coincident(g12,g0)
    c: Coincident(g2,g9)
    c: Coincident(g1,g10)
    c: Equal(g11,g12)
    c: Equal(g11,g9)
    c: Equal(g11,g10)
    c: Radius(g11) = 3
    c: Coincident(g11,g3)
    c: Coincident(g9,g3)
    c: Coincident(g10,g2)
    c: Coincident(g12,g1)
FEATURE [PartDesign::Pocket] Pocket008  label="M3 Befestigung Platine"
  BaseFeature = -> Pocket007
  Length = 4
  Length2 = 100
  Profile = -> Sketch013
  Type = 0
FEATURE [Sketcher::SketchObject] Sketch014
  MapMode = 5
  Placement = pos=(0,0,0) rot=(1,0,0;3.14159rad)
  Support = -> [DatumPlane005]
  expr: Constraints[14] = Parameter.Tiefe / 2
  expr: Constraints[13] = Parameter.Helper_Abstand_Schalenverschraubung_Aussen
  expr: Constraints[12] = Parameter.Helper_Abstand_Schalenverschraubung_Aussen
  expr: Constraints[11] = Parameter.Tiefe
  expr: Constraints[10] = Parameter.Breite
  sketch-geometry (19):
    g0: LineSegment [constr] StartX=7 StartY=-60 StartZ=0 EndX=93 EndY=-60 EndZ=0
    g1: LineSegment [constr] StartX=0 StartY=0 StartZ=0 EndX=100 EndY=0 EndZ=0
    g2: LineSegment [constr] StartX=100 StartY=0 StartZ=0 EndX=100 EndY=-120 EndZ=0
    g3: LineSegment [constr] StartX=100 StartY=-120 StartZ=0 EndX=0 EndY=-120 EndZ=0
    g4: LineSegment [constr] StartX=0 StartY=-120 StartZ=0 EndX=0 EndY=0 EndZ=0
    g5: LineSegment StartX=10.2332 StartY=-60 StartZ=0 EndX=8.61658 EndY=-57.2 EndZ=0
    g6: LineSegment StartX=8.61658 StartY=-57.2 StartZ=0 EndX=5.38342 EndY=-57.2 EndZ=0
    g7: LineSegment StartX=5.38342 StartY=-57.2 StartZ=0 EndX=3.76684 EndY=-60 EndZ=0
    g8: LineSegment StartX=3.76684 StartY=-60 StartZ=0 EndX=5.38342 EndY=-62.8 EndZ=0
    g9: LineSegment StartX=5.38342 StartY=-62.8 StartZ=0 EndX=8.61658 EndY=-62.8 EndZ=0
    g10: LineSegment StartX=8.61658 StartY=-62.8 StartZ=0 EndX=10.2332 EndY=-60 EndZ=0
    g11: Circle [constr] CenterX=7 CenterY=-60 CenterZ=0 NormalX=0 NormalY=0 NormalZ=1 AngleXU=0 Radius=3.23316
    g12: LineSegment StartX=94.6166 StartY=-62.8 StartZ=0 EndX=96.2332 EndY=-60 EndZ=0
    g13: LineSegment StartX=96.2332 StartY=-60 StartZ=0 EndX=94.6166 EndY=-57.2 EndZ=0
    g14: LineSegment StartX=94.6166 StartY=-57.2 StartZ=0 EndX=91.3834 EndY=-57.2 EndZ=0
    g15: LineSegment StartX=91.3834 StartY=-57.2 StartZ=0 EndX=89.7668 EndY=-60 EndZ=0
    g16: LineSegment StartX=89.7668 StartY=-60 StartZ=0 EndX=91.3834 EndY=-62.8 EndZ=0
    g17: LineSegment StartX=91.3834 StartY=-62.8 StartZ=0 EndX=94.6166 EndY=-62.8 EndZ=0
    g18: Circle [constr] CenterX=93 CenterY=-60 CenterZ=0 NormalX=0 NormalY=0 NormalZ=1 AngleXU=0 Radius=3.23316
  constraints (47):
    c: Horizontal(g0)
    c: Coincident(g1,g2)
    c: Coincident(g2,g3)
    c: Coincident(g3,g4)
    c: Coincident(g4,g1)
    c: Horizontal(g1)
    c: Horizontal(g3)
    c: Vertical(g2)
    c: Vertical(g4)
    c: Coincident(g-1,g1)
    c: DistanceX(g-1,g1) = 100
    c: DistanceY(g3,g-1) = 120
    c: DistanceX(g-1,g0) = 7
    c: DistanceX(g0,g1) = 7
    c: DistanceY(g3,g0) = 60
    c: Coincident(g5,g6)
    c: Coincident(g6,g7)
    c: Coincident(g7,g8)
    c: Coincident(g8,g9)
    c: Coincident(g9,g10)
    c: Coincident(g10,g5)
    c: Equal(g5, g6-g10) x5
    c: PointOnObject(g5,g11)
    c: PointOnObject(g6,g11)
    c: PointOnObject(g7,g11)
    c: PointOnObject(g8,g11)
    c: PointOnObject(g9,g11)
    c: PointOnObject(g10,g11)
    c: Coincident(g12,g13)
    c: Coincident(g13,g14)
    c: Coincident(g14,g15)
    c: Coincident(g15,g16)
    c: Coincident(g16,g17)
    c: Coincident(g17,g12)
    c: Equal(g12, g13-g17) x5
    c: PointOnObject(g12,g18)
    c: PointOnObject(g13,g18)
    c: PointOnObject(g14,g18)
    c: PointOnObject(g15,g18)
    c: PointOnObject(g16,g18)
    c: PointOnObject(g17,g18)
    c: Coincident(g0,g18)
    c: Coincident(g0,g11)
    c: Horizontal(g6)
    c: Horizontal(g14)
    c: DistanceY(g9,g5) = 5.6
    c: DistanceY(g12,g13) = 5.6
FEATURE [PartDesign::Pocket] Pocket009  label="M3 Verschraubung Unterteil Oberteil"
  BaseFeature = -> Pocket008
  Length = 20
  Length2 = 100
  Profile = -> Sketch014
  Type = 0
  expr: Length = Parameter.Hoehe - 5
FEATURE [Sketcher::SketchObject] Sketch015
  MapMode = 5
  Placement = pos=(0,0,0) rot=(1,0,0;3.14159rad)
  Support = -> [DatumPlane005]
  expr: Constraints[149] = Parameter.Luftschlitz_Tiefe_Boden
  expr: Constraints[148] = Parameter.Luftschlitz_Breite_Boden
  expr: Constraints[113] = Parameter.Luftschlitz_Tiefe_Boden
  expr: Constraints[81] = Parameter.Tiefe
  expr: Constraints[112] = Parameter.Luftschlitz_Breite_Boden
  expr: Constraints[80] = Parameter.Breite
  expr: Constraints[55] = Parameter.Luftschlitz_Tiefe_Boden
  expr: Constraints[54] = Parameter.Luftschlitz_Breite_Boden
  sketch-geometry (52):
    g0: LineSegment StartX=0 StartY=-25 StartZ=0 EndX=30 EndY=-25 EndZ=0
    g1: LineSegment StartX=30 StartY=-25 StartZ=0 EndX=30 EndY=-28 EndZ=0
    g2: LineSegment StartX=30 StartY=-28 StartZ=0 EndX=0 EndY=-28 EndZ=0
    g3: LineSegment StartX=0 StartY=-28 StartZ=0 EndX=0 EndY=-25 EndZ=0
    g4: LineSegment StartX=0 StartY=-31 StartZ=0 EndX=30 EndY=-31 EndZ=0
    g5: LineSegment StartX=30 StartY=-31 StartZ=0 EndX=30 EndY=-34 EndZ=0
    g6: LineSegment StartX=30 StartY=-34 StartZ=0 EndX=0 EndY=-34 EndZ=0
    g7: LineSegment StartX=0 StartY=-34 StartZ=0 EndX=0 EndY=-31 EndZ=0
    g8: LineSegment StartX=0 StartY=-40 StartZ=0 EndX=30 EndY=-40 EndZ=0
    g9: LineSegment StartX=30 StartY=-40 StartZ=0 EndX=30 EndY=-37 EndZ=0
    g10: LineSegment StartX=30 StartY=-37 StartZ=0 EndX=0 EndY=-37 EndZ=0
    g11: LineSegment StartX=0 StartY=-37 StartZ=0 EndX=0 EndY=-40 EndZ=0
    g12: LineSegment StartX=0 StartY=-75 StartZ=0 EndX=30 EndY=-75 EndZ=0
    g13: LineSegment StartX=30 StartY=-75 StartZ=0 EndX=30 EndY=-78 EndZ=0
    g14: LineSegment StartX=30 StartY=-78 StartZ=0 EndX=0 EndY=-78 EndZ=0
    g15: LineSegment StartX=0 StartY=-78 StartZ=0 EndX=0 EndY=-75 EndZ=0
    g16: LineSegment StartX=0 StartY=-81 StartZ=0 EndX=30 EndY=-81 EndZ=0
    g17: LineSegment StartX=30 StartY=-81 StartZ=0 EndX=30 EndY=-84 EndZ=0
    g18: LineSegment StartX=30 StartY=-84 StartZ=0 EndX=0 EndY=-84 EndZ=0
    g19: LineSegment StartX=0 StartY=-84 StartZ=0 EndX=0 EndY=-81 EndZ=0
    g20: LineSegment StartX=0 StartY=-90 StartZ=0 EndX=30 EndY=-90 EndZ=0
    g21: LineSegment StartX=30 StartY=-90 StartZ=0 EndX=30 EndY=-87 EndZ=0
    g22: LineSegment StartX=30 StartY=-87 StartZ=0 EndX=0 EndY=-87 EndZ=0
    g23: LineSegment StartX=0 StartY=-87 StartZ=0 EndX=0 EndY=-90 EndZ=0
    g24: LineSegment [constr] StartX=0 StartY=0 StartZ=0 EndX=100 EndY=0 EndZ=0
    g25: LineSegment [constr] StartX=100 StartY=0 StartZ=0 EndX=100 EndY=-120 EndZ=0
    g26: LineSegment [constr] StartX=100 StartY=-120 StartZ=0 EndX=0 EndY=-120 EndZ=0
    g27: LineSegment [constr] StartX=0 StartY=-120 StartZ=0 EndX=0 EndY=0 EndZ=0
    g28: LineSegment StartX=100 StartY=-25 StartZ=0 EndX=70 EndY=-25 EndZ=0
    g29: LineSegment StartX=70 StartY=-25 StartZ=0 EndX=70 EndY=-28 EndZ=0
    g30: LineSegment StartX=70 StartY=-28 StartZ=0 EndX=100 EndY=-28 EndZ=0
    g31: LineSegment StartX=100 StartY=-28 StartZ=0 EndX=100 EndY=-25 EndZ=0
    g32: LineSegment StartX=100 StartY=-31 StartZ=0 EndX=70 EndY=-31 EndZ=0
    g33: LineSegment StartX=70 StartY=-31 StartZ=0 EndX=70 EndY=-34 EndZ=0
    g34: LineSegment StartX=70 StartY=-34 StartZ=0 EndX=100 EndY=-34 EndZ=0
    g35: LineSegment StartX=100 StartY=-34 StartZ=0 EndX=100 EndY=-31 EndZ=0
    g36: LineSegment StartX=100 StartY=-37 StartZ=0 EndX=70 EndY=-37 EndZ=0
    g37: LineSegment StartX=70 StartY=-37 StartZ=0 EndX=70 EndY=-40 EndZ=0
    g38: LineSegment StartX=70 StartY=-40 StartZ=0 EndX=100 EndY=-40 EndZ=0
    g39: LineSegment StartX=100 StartY=-40 StartZ=0 EndX=100 EndY=-37 EndZ=0
    g40: LineSegment StartX=100 StartY=-75 StartZ=0 EndX=70 EndY=-75 EndZ=0
    g41: LineSegment StartX=70 StartY=-75 StartZ=0 EndX=70 EndY=-78 EndZ=0
    g42: LineSegment StartX=70 StartY=-78 StartZ=0 EndX=100 EndY=-78 EndZ=0
    g43: LineSegment StartX=100 StartY=-78 StartZ=0 EndX=100 EndY=-75 EndZ=0
    g44: LineSegment StartX=100 StartY=-81 StartZ=0 EndX=70 EndY=-81 EndZ=0
    g45: LineSegment StartX=70 StartY=-81 StartZ=0 EndX=70 EndY=-84 EndZ=0
    g46: LineSegment StartX=70 StartY=-84 StartZ=0 EndX=100 EndY=-84 EndZ=0
    g47: LineSegment StartX=100 StartY=-84 StartZ=0 EndX=100 EndY=-81 EndZ=0
    g48: LineSegment StartX=100 StartY=-87 StartZ=0 EndX=70 EndY=-87 EndZ=0
    g49: LineSegment StartX=70 StartY=-87 StartZ=0 EndX=70 EndY=-90 EndZ=0
    g50: LineSegment StartX=70 StartY=-90 StartZ=0 EndX=100 EndY=-90 EndZ=0
    g51: LineSegment StartX=100 StartY=-90 StartZ=0 EndX=100 EndY=-87 EndZ=0
  constraints (155):
    c: Coincident(g0,g1)
    c: Coincident(g1,g2)
    c: Coincident(g2,g3)
    c: Coincident(g3,g0)
    c: Horizontal(g0)
    c: Horizontal(g2)
    c: Vertical(g1)
    c: Vertical(g3)
    c: PointOnObject(g0,g-2)
    c: Coincident(g4,g5)
    c: Coincident(g5,g6)
    c: Coincident(g6,g7)
    c: Coincident(g7,g4)
    c: Horizontal(g4)
    c: Horizontal(g6)
    c: Vertical(g5)
    c: Vertical(g7)
    c: PointOnObject(g4,g-2)
    c: Coincident(g8,g9)
    c: Coincident(g9,g10)
    c: Coincident(g10,g11)
    c: Coincident(g11,g8)
    c: Horizontal(g8)
    c: Horizontal(g10)
    c: Vertical(g9)
    c: Vertical(g11)
    c: PointOnObject(g8,g-2)
    c: Coincident(g12,g13)
    c: Coincident(g13,g14)
    c: Coincident(g14,g15)
    c: Coincident(g15,g12)
    c: Horizontal(g12)
    c: Horizontal(g14)
    c: Vertical(g13)
    c: Vertical(g15)
    c: PointOnObject(g12,g-2)
    c: Coincident(g16,g17)
    c: Coincident(g17,g18)
    c: Coincident(g18,g19)
    c: Coincident(g19,g16)
    c: Horizontal(g16)
    c: Horizontal(g18)
    c: Vertical(g17)
    c: Vertical(g19)
    c: PointOnObject(g16,g-2)
    c: Coincident(g20,g21)
    c: Coincident(g21,g22)
    c: Coincident(g22,g23)
    c: Coincident(g23,g20)
    c: Horizontal(g20)
    c: Horizontal(g22)
    c: Vertical(g21)
    c: Vertical(g23)
    c: PointOnObject(g20,g-2)
    c: DistanceX(g0,g0) = 30
    c: DistanceY(g1,g0) = 3
    c: DistanceY(g4,g2) = 3
    c: DistanceY(g10,g6) = 3
    c: Equal(g0,g4)
    c: Equal(g0,g10)
    c: Equal(g1,g5)
    c: Equal(g1,g9)
    c: DistanceY(g0,g-1) = 25
    c: Equal(g10,g12)
    c: Equal(g10,g16)
    c: Equal(g10,g22)
    c: Equal(g9,g13)
    c: Equal(g9,g17)
    c: Equal(g9,g21)
    c: DistanceY(g16,g14) = 3
    c: DistanceY(g22,g18) = 3
    c: Coincident(g24,g25)
    c: Coincident(g25,g26)
    c: Coincident(g26,g27)
    c: Coincident(g27,g24)
    c: Horizontal(g24)
    c: Horizontal(g26)
    c: Vertical(g25)
    c: Vertical(g27)
    c: Coincident(g-1,g24)
    c: DistanceX(g-1,g24) = 100
    c: DistanceY(g25,g24) = 120
    c: DistanceY(g26,g20) = 30
    c: Coincident(g28,g29)
    c: Coincident(g29,g30)
    c: Coincident(g30,g31)
    c: Coincident(g31,g28)
    c: Horizontal(g28)
    c: Horizontal(g30)
    c: Vertical(g29)
    c: Vertical(g31)
    c: PointOnObject(g28,g25)
    c: Coincident(g32,g33)
    c: Coincident(g33,g34)
    c: Coincident(g34,g35)
    c: Coincident(g35,g32)
    c: Horizontal(g32)
    c: Horizontal(g34)
    c: Vertical(g33)
    c: Vertical(g35)
    c: PointOnObject(g32,g25)
    c: Coincident(g36,g37)
    c: Coincident(g37,g38)
    c: Coincident(g38,g39)
    c: Coincident(g39,g36)
    c: Horizontal(g36)
    c: Horizontal(g38)
    c: Vertical(g37)
    c: Vertical(g39)
    c: PointOnObject(g36,g25)
    c: DistanceY(g32,g30) = 3
    c: DistanceY(g36,g34) = 3
    c: DistanceX(g28,g28) = 30
    c: DistanceY(g29,g28) = 3
    c: Equal(g28,g32)
    c: Equal(g28,g36)
    c: Equal(g29,g33)
    c: Equal(g29,g37)
    c: DistanceY(g28,g24) = 25
    c: Coincident(g40,g41)
    c: Coincident(g41,g42)
    c: Coincident(g42,g43)
    c: Coincident(g43,g40)
    c: Horizontal(g40)
    c: Horizontal(g42)
    c: Vertical(g41)
    c: Vertical(g43)
    c: PointOnObject(g40,g25)
    c: Coincident(g44,g45)
    c: Coincident(g45,g46)
    c: Coincident(g46,g47)
    c: Coincident(g47,g44)
    c: Horizontal(g44)
    c: Horizontal(g46)
    c: Vertical(g45)
    c: Vertical(g47)
    c: PointOnObject(g44,g25)
    c: Coincident(g48,g49)
    c: Coincident(g49,g50)
    c: Coincident(g50,g51)
    c: Coincident(g51,g48)
    c: Horizontal(g48)
    c: Horizontal(g50)
    c: Vertical(g49)
    c: Vertical(g51)
    c: PointOnObject(g48,g25)
    c: DistanceY(g44,g42) = 3
    c: DistanceY(g48,g46) = 3
    c: DistanceX(g40,g40) = 30
    c: DistanceY(g41,g40) = 3
    c: Equal(g40,g44)
    c: Equal(g40,g48)
    c: Equal(g41,g45)
    c: Equal(g41,g49)
    c: DistanceY(g25,g50) = 30
FEATURE [PartDesign::Pocket] Pocket010  label="Lüftungsschlitze"
  BaseFeature = -> Pocket009
  Length = 10
  Length2 = 100
  Profile = -> Sketch015
  Type = 0
  expr: Length = Parameter.Luftschlitz_Hoehe_Boden
FEATURE [PartDesign::Pad] Pad010
  BaseFeature = -> Pocket006
  Length = 5
  Length2 = 100
  Profile = -> Sketch011
  Type = 0
FEATURE [PartDesign::Fillet] Fillet
  Base = -> Pocket010 [Edge415,Edge413]
  BaseFeature = -> Pocket010
  Radius = 1
FEATURE [Sketcher::SketchObject] Sketch026
  MapMode = 5
  Placement = pos=(0,0,25) rot=(0,0,1;0rad)
  Support = -> [Fillet]
  expr: Constraints[35] = Parameter.Helper_Nut_Feder_Breite_Unterteil
  expr: Constraints[34] = Parameter.Helper_Nut_Feder_Breite_Unterteil
  expr: Constraints[33] = (Parameter.Wandstaerke - Parameter.Helper_Nut_Feder_Breite_Unterteil) / 2
  expr: Constraints[32] = (Parameter.Wandstaerke - Parameter.Helper_Nut_Feder_Breite_Unterteil) / 2
  expr: Constraints[11] = Parameter.Tiefe - 2 * Parameter.Nut_Feder_Entfernung_Vorne_Hinten - 4
  expr: Constraints[10] = Parameter.Breite
  expr: Constraints[9] = Parameter.Nut_Feder_Entfernung_Vorne_Hinten + 2
  sketch-geometry (12):
    g0: LineSegment [constr] StartX=0 StartY=12 StartZ=0 EndX=100 EndY=12 EndZ=0
    g1: LineSegment [constr] StartX=100 StartY=12 StartZ=0 EndX=100 EndY=108 EndZ=0
    g2: LineSegment [constr] StartX=100 StartY=108 StartZ=0 EndX=0 EndY=108 EndZ=0
    g3: LineSegment [constr] StartX=0 StartY=108 StartZ=0 EndX=0 EndY=12 EndZ=0
    g4: LineSegment StartX=1.05 StartY=108 StartZ=0 EndX=1.95 EndY=108 EndZ=0
    g5: LineSegment StartX=1.95 StartY=108 StartZ=0 EndX=1.95 EndY=12 EndZ=0
    g6: LineSegment StartX=1.95 StartY=12 StartZ=0 EndX=1.05 EndY=12 EndZ=0
    g7: LineSegment StartX=1.05 StartY=12 StartZ=0 EndX=1.05 EndY=108 EndZ=0
    g8: LineSegment StartX=98.05 StartY=108 StartZ=0 EndX=98.95 EndY=108 EndZ=0
    g9: LineSegment StartX=98.95 StartY=108 StartZ=0 EndX=98.95 EndY=12 EndZ=0
    g10: LineSegment StartX=98.95 StartY=12 StartZ=0 EndX=98.05 EndY=12 EndZ=0
    g11: LineSegment StartX=98.05 StartY=12 StartZ=0 EndX=98.05 EndY=108 EndZ=0
  constraints (36):
    c: Coincident(g0,g1)
    c: Coincident(g1,g2)
    c: Coincident(g2,g3)
    c: Coincident(g3,g0)
    c: Horizontal(g0)
    c: Horizontal(g2)
    c: Vertical(g1)
    c: Vertical(g3)
    c: PointOnObject(g0,g-2)
    c: DistanceY(g-1,g0) = 12
    c: DistanceX(g0,g0) = 100
    c: DistanceY(g0,g1) = 96
    c: Coincident(g4,g5)
    c: Coincident(g5,g6)
    c: Coincident(g6,g7)
    c: Coincident(g7,g4)
    c: Horizontal(g4)
    c: Horizontal(g6)
    c: Vertical(g5)
    c: Vertical(g7)
    c: PointOnObject(g4,g2)
    c: PointOnObject(g5,g0)
    c: Coincident(g8,g9)
    c: Coincident(g9,g10)
    c: Coincident(g10,g11)
    c: Coincident(g11,g8)
    c: Horizontal(g8)
    c: Horizontal(g10)
    c: Vertical(g9)
    c: Vertical(g11)
    c: PointOnObject(g8,g2)
    c: PointOnObject(g9,g0)
    c: DistanceX(g2,g4) = 1.05
    c: DistanceX(g8,g1) = 1.05
    c: DistanceX(g4,g4) = 0.9
    c: DistanceX(g8,g8) = 0.9
FEATURE [PartDesign::Pad] Pad013  label="Feder Unterteil"
  BaseFeature = -> Fillet
  Length = 2
  Length2 = 100
  Profile = -> Sketch026
  Type = 0
FEATURE [Sketcher::SketchObject] Sketch027
  MapMode = 5
  Placement = pos=(0,0,3) rot=(0,0,1;0rad)
  Support = -> [Fillet]
  expr: Constraints[11] = (Parameter.Tiefe - 75) / 2.2999999999999998
  expr: Constraints[10] = (Parameter.Breite - 70) / 2
  sketch-geometry (4):
    g0: LineSegment StartX=15 StartY=94.5652 StartZ=0 EndX=85 EndY=94.5652 EndZ=0
    g1: LineSegment StartX=85 StartY=94.5652 StartZ=0 EndX=85 EndY=19.5652 EndZ=0
    g2: LineSegment StartX=85 StartY=19.5652 StartZ=0 EndX=15 EndY=19.5652 EndZ=0
    g3: LineSegment StartX=15 StartY=19.5652 StartZ=0 EndX=15 EndY=94.5652 EndZ=0
  constraints (12):
    c: Coincident(g0,g1)
    c: Coincident(g1,g2)
    c: Coincident(g2,g3)
    c: Coincident(g3,g0)
    c: Horizontal(g0)
    c: Horizontal(g2)
    c: Vertical(g1)
    c: Vertical(g3)
    c: DistanceX(g2,g1) = 70
    c: DistanceY(g2,g0) = 75
    c: DistanceX(g-1,g2) = 15
    c: DistanceY(g-1,g2) = 19.5652
FEATURE [PartDesign::Pocket] Pocket020  label="Minimize Material"
  BaseFeature = -> Pad013
  Length = 2
  Length2 = 100
  Profile = -> Sketch027
  Type = 0
